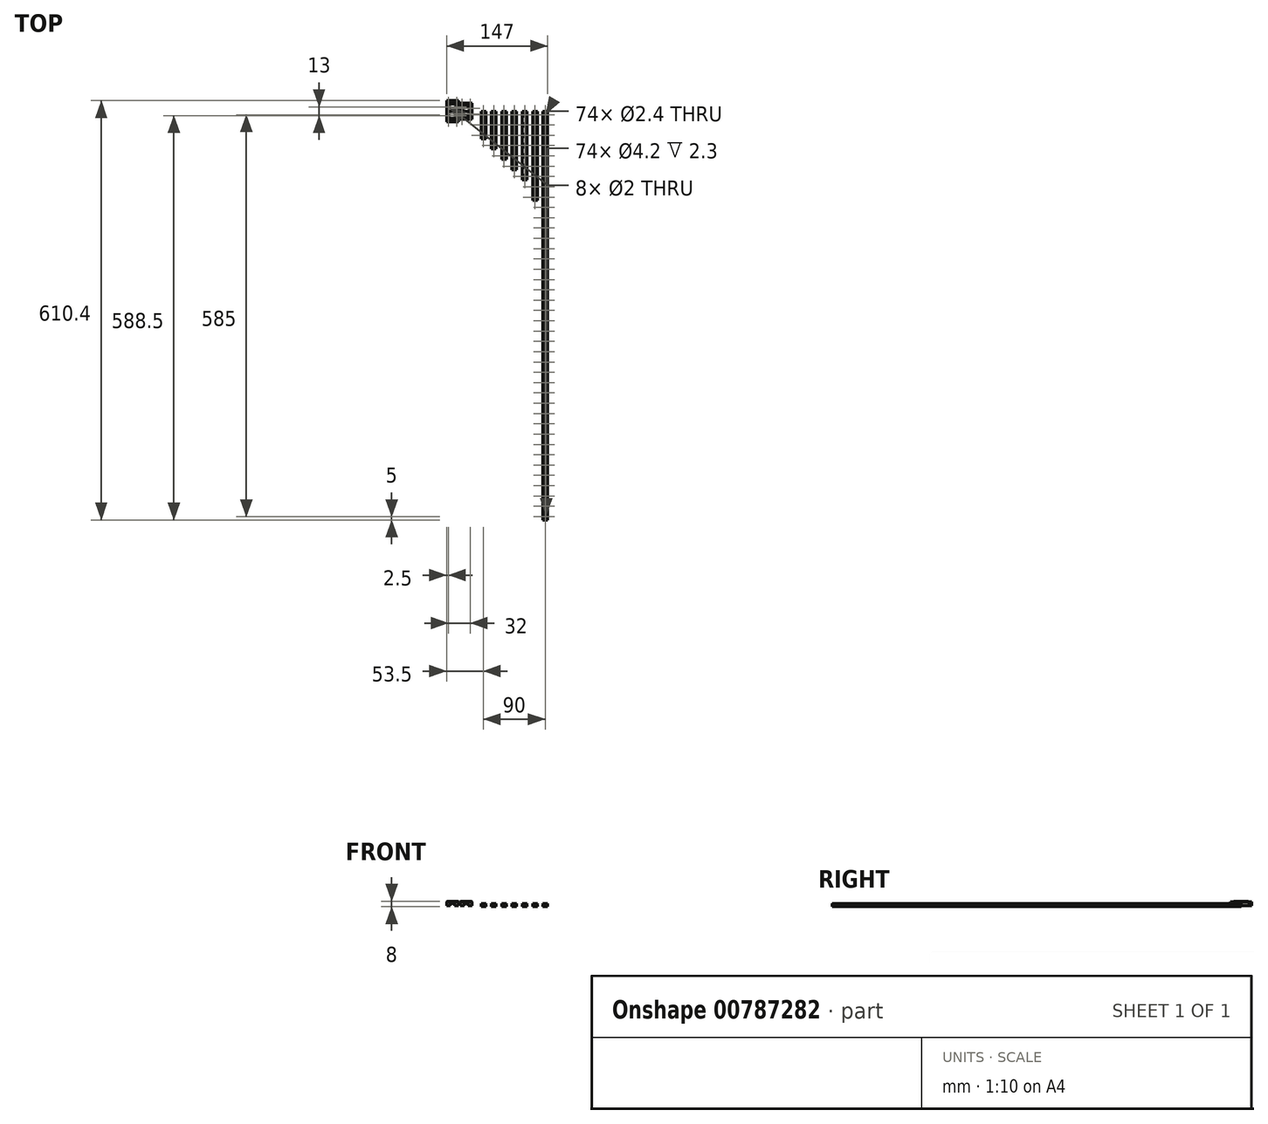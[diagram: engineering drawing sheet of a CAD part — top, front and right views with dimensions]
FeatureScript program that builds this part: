
annotation { "Feature Type Name" : "Feature", "Feature Type Description" : "" }
export const myFeature = defineFeature(function(context is Context, id is Id, definition is map)
    precondition{}
    {
        {
            var Q0;
            Q0=qCreatedBy(makeId("Front.planeOp"),FACE);
            var sketch = newSketch(context, id + "F0", { "sketchPlane" : qUnion([Q0])});
            skPoint(sketch, "E0.middle", {"position": v(0, 0) * mm});
            skLineSegment(sketch, "E1.bottom", {"start": v(3.22, -2.4) * mm, "end": v(-3.22, -2.4) * mm});
            skLineSegment(sketch, "E1.top", {"start": v(3.22, 2.4) * mm, "end": v(-3.22, 2.4) * mm});
            skLineSegment(sketch, "E1.left", {"start": v(3.5, -2.12) * mm, "end": v(3.5, 0.1) * mm});
            skLineSegment(sketch, "E1.right", {"start": v(-3.5, -2.12) * mm, "end": v(-3.5, 0.1) * mm});
            skArc(sketch, "E2", {"start": v(-3.5, 0.1) * mm, "mid": v(-3.23, 0.26) * mm, "end": v(-3.04, 0.51) * mm});
            skArc(sketch, "E3", {"start": v(3.5, 1.58) * mm, "mid": v(3.23, 1.42) * mm, "end": v(3.04, 1.17) * mm});
            skLineSegment(sketch, "E4", {"start": v(2.6, 1.16) * mm, "end": v(3.04, 1.16) * mm});
            skLineSegment(sketch, "E5", {"start": v(2.6, 0.51) * mm, "end": v(3.04, 0.51) * mm});
            skLineSegment(sketch, "E6", {"start": v(-2.6, 0.51) * mm, "end": v(-3.04, 0.51) * mm});
            skLineSegment(sketch, "E7", {"start": v(-2.6, 1.16) * mm, "end": v(-3.04, 1.16) * mm});
            skLineSegment(sketch, "E8", {"start": v(-3.5, 2.12) * mm, "end": v(-3.22, 2.4) * mm});
            skLineSegment(sketch, "E9.MirrorCS", {"start": v(3.5, 2.12) * mm, "end": v(3.22, 2.4) * mm});
            skLineSegment(sketch, "E10.MirrorCS", {"start": v(3.5, -2.12) * mm, "end": v(3.22, -2.4) * mm});
            skLineSegment(sketch, "E11.MirrorCS", {"start": v(-3.5, -2.12) * mm, "end": v(-3.22, -2.4) * mm});
            skPoint(sketch, "E12.orphan", {"position": v(-3.5, 2.4) * mm});
            skLineSegment(sketch, "E13.trimOffspring", {"start": v(-3.5, 1.58) * mm, "end": v(-3.5, 2.12) * mm});
            skArc(sketch, "E14.trimOffspring", {"start": v(-3.04, 1.17) * mm, "mid": v(-3.23, 1.42) * mm, "end": v(-3.5, 1.58) * mm});
            skPoint(sketch, "E15.orphan", {"position": v(3.5, 2.4) * mm});
            skLineSegment(sketch, "E16.trimOffspring", {"start": v(3.5, 1.58) * mm, "end": v(3.5, 2.12) * mm});
            skArc(sketch, "E17.trimOffspring", {"start": v(3.04, 0.51) * mm, "mid": v(3.23, 0.26) * mm, "end": v(3.5, 0.1) * mm});
            skPoint(sketch, "E18.orphan", {"position": v(3.5, -2.4) * mm});
            skPoint(sketch, "E19.orphan", {"position": v(-3.5, -2.4) * mm});
            skLineSegment(sketch, "E20", {"start": v(-2.6, 1.16) * mm, "end": v(-2.6, 0.51) * mm});
            skLineSegment(sketch, "E21", {"start": v(2.6, 1.16) * mm, "end": v(2.6, 0.51) * mm});
            skLineSegment(sketch, "E22", {"start": v(-3.74, 0.84) * mm, "end": v(3.74, 0.84) * mm, "construction": true});
            skLineSegment(sketch, "E23.1.0.0", {"start": v(11.26, 0.84) * mm, "end": v(18.74, 0.84) * mm, "construction": true});
            skLineSegment(sketch, "E23.1.0.1", {"start": v(11.5, -2.12) * mm, "end": v(11.5, 0.1) * mm});
            skLineSegment(sketch, "E23.1.0.2", {"start": v(18.5, -2.12) * mm, "end": v(18.5, 0.1) * mm});
            skLineSegment(sketch, "E23.1.0.3", {"start": v(18.22, -2.4) * mm, "end": v(11.78, -2.4) * mm});
            skLineSegment(sketch, "E23.1.0.4", {"start": v(18.22, 2.4) * mm, "end": v(11.78, 2.4) * mm});
            skPoint(sketch, "E23.1.0.5", {"position": v(15, 0) * mm});
            skPoint(sketch, "E23.1.0.6", {"position": v(11.5, -2.4) * mm});
            skPoint(sketch, "E23.1.0.7", {"position": v(11.5, 2.4) * mm});
            skPoint(sketch, "E23.1.0.8", {"position": v(18.5, 2.4) * mm});
            skPoint(sketch, "E23.1.0.9", {"position": v(18.5, -2.4) * mm});
            skPoint(sketch, "E23.1.0.10", {"position": v(15, 0) * mm});
            skLineSegment(sketch, "E23.1.0.11", {"start": v(18.5, -2.12) * mm, "end": v(18.22, -2.4) * mm});
            skLineSegment(sketch, "E23.1.0.12", {"start": v(18.5, 2.12) * mm, "end": v(18.22, 2.4) * mm});
            skLineSegment(sketch, "E23.1.0.13", {"start": v(11.5, -2.12) * mm, "end": v(11.78, -2.4) * mm});
            skLineSegment(sketch, "E23.1.0.14", {"start": v(12.4, 1.16) * mm, "end": v(11.96, 1.16) * mm});
            skLineSegment(sketch, "E23.1.0.15", {"start": v(11.5, 1.58) * mm, "end": v(11.5, 2.12) * mm});
            skLineSegment(sketch, "E23.1.0.16", {"start": v(18.5, 1.58) * mm, "end": v(18.5, 2.12) * mm});
            skArc(sketch, "E23.1.0.17", {"start": v(18.04, 0.51) * mm, "mid": v(18.23, 0.26) * mm, "end": v(18.5, 0.1) * mm});
            skLineSegment(sketch, "E23.1.0.18", {"start": v(12.4, 1.16) * mm, "end": v(12.4, 0.51) * mm});
            skLineSegment(sketch, "E23.1.0.19", {"start": v(17.6, 0.51) * mm, "end": v(18.04, 0.51) * mm});
            skLineSegment(sketch, "E23.1.0.20", {"start": v(12.4, 0.51) * mm, "end": v(11.96, 0.51) * mm});
            skArc(sketch, "E23.1.0.21", {"start": v(11.5, 0.1) * mm, "mid": v(11.77, 0.26) * mm, "end": v(11.96, 0.51) * mm});
            skLineSegment(sketch, "E23.1.0.22", {"start": v(11.5, 2.12) * mm, "end": v(11.78, 2.4) * mm});
            skArc(sketch, "E23.1.0.23", {"start": v(11.96, 1.17) * mm, "mid": v(11.77, 1.42) * mm, "end": v(11.5, 1.58) * mm});
            skLineSegment(sketch, "E23.1.0.24", {"start": v(17.6, 1.16) * mm, "end": v(18.04, 1.16) * mm});
            skArc(sketch, "E23.1.0.25", {"start": v(18.5, 1.58) * mm, "mid": v(18.23, 1.42) * mm, "end": v(18.04, 1.17) * mm});
            skArc(sketch, "E23.1.0.26", {"start": v(18.04, 0.51) * mm, "mid": v(18.23, 0.26) * mm, "end": v(18.5, 0.1) * mm});
            skLineSegment(sketch, "E23.1.0.27", {"start": v(17.6, 1.16) * mm, "end": v(17.6, 0.51) * mm});
            skLineSegment(sketch, "E23.2.0.0", {"start": v(26.26, 0.84) * mm, "end": v(33.74, 0.84) * mm, "construction": true});
            skLineSegment(sketch, "E23.2.0.1", {"start": v(26.5, -2.12) * mm, "end": v(26.5, 0.1) * mm});
            skLineSegment(sketch, "E23.2.0.2", {"start": v(33.5, -2.12) * mm, "end": v(33.5, 0.1) * mm});
            skLineSegment(sketch, "E23.2.0.3", {"start": v(33.22, -2.4) * mm, "end": v(26.78, -2.4) * mm});
            skLineSegment(sketch, "E23.2.0.4", {"start": v(33.22, 2.4) * mm, "end": v(26.78, 2.4) * mm});
            skPoint(sketch, "E23.2.0.5", {"position": v(30, 0) * mm});
            skPoint(sketch, "E23.2.0.6", {"position": v(26.5, -2.4) * mm});
            skPoint(sketch, "E23.2.0.7", {"position": v(26.5, 2.4) * mm});
            skPoint(sketch, "E23.2.0.8", {"position": v(33.5, 2.4) * mm});
            skPoint(sketch, "E23.2.0.9", {"position": v(33.5, -2.4) * mm});
            skPoint(sketch, "E23.2.0.10", {"position": v(30, 0) * mm});
            skLineSegment(sketch, "E23.2.0.11", {"start": v(33.5, -2.12) * mm, "end": v(33.22, -2.4) * mm});
            skLineSegment(sketch, "E23.2.0.12", {"start": v(33.5, 2.12) * mm, "end": v(33.22, 2.4) * mm});
            skLineSegment(sketch, "E23.2.0.13", {"start": v(26.5, -2.12) * mm, "end": v(26.78, -2.4) * mm});
            skLineSegment(sketch, "E23.2.0.14", {"start": v(27.4, 1.16) * mm, "end": v(26.96, 1.16) * mm});
            skLineSegment(sketch, "E23.2.0.15", {"start": v(26.5, 1.58) * mm, "end": v(26.5, 2.12) * mm});
            skLineSegment(sketch, "E23.2.0.16", {"start": v(33.5, 1.58) * mm, "end": v(33.5, 2.12) * mm});
            skArc(sketch, "E23.2.0.17", {"start": v(33.04, 0.51) * mm, "mid": v(33.23, 0.26) * mm, "end": v(33.5, 0.1) * mm});
            skLineSegment(sketch, "E23.2.0.18", {"start": v(27.4, 1.16) * mm, "end": v(27.4, 0.51) * mm});
            skLineSegment(sketch, "E23.2.0.19", {"start": v(32.6, 0.51) * mm, "end": v(33.04, 0.51) * mm});
            skLineSegment(sketch, "E23.2.0.20", {"start": v(27.4, 0.51) * mm, "end": v(26.96, 0.51) * mm});
            skArc(sketch, "E23.2.0.21", {"start": v(26.5, 0.1) * mm, "mid": v(26.77, 0.26) * mm, "end": v(26.96, 0.51) * mm});
            skLineSegment(sketch, "E23.2.0.22", {"start": v(26.5, 2.12) * mm, "end": v(26.78, 2.4) * mm});
            skArc(sketch, "E23.2.0.23", {"start": v(26.96, 1.17) * mm, "mid": v(26.77, 1.42) * mm, "end": v(26.5, 1.58) * mm});
            skLineSegment(sketch, "E23.2.0.24", {"start": v(32.6, 1.16) * mm, "end": v(33.04, 1.16) * mm});
            skArc(sketch, "E23.2.0.25", {"start": v(33.5, 1.58) * mm, "mid": v(33.23, 1.42) * mm, "end": v(33.04, 1.17) * mm});
            skArc(sketch, "E23.2.0.26", {"start": v(33.04, 0.51) * mm, "mid": v(33.23, 0.26) * mm, "end": v(33.5, 0.1) * mm});
            skLineSegment(sketch, "E23.2.0.27", {"start": v(32.6, 1.16) * mm, "end": v(32.6, 0.51) * mm});
            skLineSegment(sketch, "E23.3.0.0", {"start": v(41.26, 0.84) * mm, "end": v(48.74, 0.84) * mm, "construction": true});
            skLineSegment(sketch, "E23.3.0.1", {"start": v(41.5, -2.12) * mm, "end": v(41.5, 0.1) * mm});
            skLineSegment(sketch, "E23.3.0.2", {"start": v(48.5, -2.12) * mm, "end": v(48.5, 0.1) * mm});
            skLineSegment(sketch, "E23.3.0.3", {"start": v(48.22, -2.4) * mm, "end": v(41.78, -2.4) * mm});
            skLineSegment(sketch, "E23.3.0.4", {"start": v(48.22, 2.4) * mm, "end": v(41.78, 2.4) * mm});
            skPoint(sketch, "E23.3.0.5", {"position": v(45, 0) * mm});
            skPoint(sketch, "E23.3.0.6", {"position": v(41.5, -2.4) * mm});
            skPoint(sketch, "E23.3.0.7", {"position": v(41.5, 2.4) * mm});
            skPoint(sketch, "E23.3.0.8", {"position": v(48.5, 2.4) * mm});
            skPoint(sketch, "E23.3.0.9", {"position": v(48.5, -2.4) * mm});
            skPoint(sketch, "E23.3.0.10", {"position": v(45, 0) * mm});
            skLineSegment(sketch, "E23.3.0.11", {"start": v(48.5, -2.12) * mm, "end": v(48.22, -2.4) * mm});
            skLineSegment(sketch, "E23.3.0.12", {"start": v(48.5, 2.12) * mm, "end": v(48.22, 2.4) * mm});
            skLineSegment(sketch, "E23.3.0.13", {"start": v(41.5, -2.12) * mm, "end": v(41.78, -2.4) * mm});
            skLineSegment(sketch, "E23.3.0.14", {"start": v(42.4, 1.16) * mm, "end": v(41.96, 1.16) * mm});
            skLineSegment(sketch, "E23.3.0.15", {"start": v(41.5, 1.58) * mm, "end": v(41.5, 2.12) * mm});
            skLineSegment(sketch, "E23.3.0.16", {"start": v(48.5, 1.58) * mm, "end": v(48.5, 2.12) * mm});
            skArc(sketch, "E23.3.0.17", {"start": v(48.04, 0.51) * mm, "mid": v(48.23, 0.26) * mm, "end": v(48.5, 0.1) * mm});
            skLineSegment(sketch, "E23.3.0.18", {"start": v(42.4, 1.16) * mm, "end": v(42.4, 0.51) * mm});
            skLineSegment(sketch, "E23.3.0.19", {"start": v(47.6, 0.51) * mm, "end": v(48.04, 0.51) * mm});
            skLineSegment(sketch, "E23.3.0.20", {"start": v(42.4, 0.51) * mm, "end": v(41.96, 0.51) * mm});
            skArc(sketch, "E23.3.0.21", {"start": v(41.5, 0.1) * mm, "mid": v(41.77, 0.26) * mm, "end": v(41.96, 0.51) * mm});
            skLineSegment(sketch, "E23.3.0.22", {"start": v(41.5, 2.12) * mm, "end": v(41.78, 2.4) * mm});
            skArc(sketch, "E23.3.0.23", {"start": v(41.96, 1.17) * mm, "mid": v(41.77, 1.42) * mm, "end": v(41.5, 1.58) * mm});
            skLineSegment(sketch, "E23.3.0.24", {"start": v(47.6, 1.16) * mm, "end": v(48.04, 1.16) * mm});
            skArc(sketch, "E23.3.0.25", {"start": v(48.5, 1.58) * mm, "mid": v(48.23, 1.42) * mm, "end": v(48.04, 1.17) * mm});
            skArc(sketch, "E23.3.0.26", {"start": v(48.04, 0.51) * mm, "mid": v(48.23, 0.26) * mm, "end": v(48.5, 0.1) * mm});
            skLineSegment(sketch, "E23.3.0.27", {"start": v(47.6, 1.16) * mm, "end": v(47.6, 0.51) * mm});
            skLineSegment(sketch, "E23.4.0.0", {"start": v(56.26, 0.84) * mm, "end": v(63.74, 0.84) * mm, "construction": true});
            skLineSegment(sketch, "E23.4.0.1", {"start": v(56.5, -2.12) * mm, "end": v(56.5, 0.1) * mm});
            skLineSegment(sketch, "E23.4.0.2", {"start": v(63.5, -2.12) * mm, "end": v(63.5, 0.1) * mm});
            skLineSegment(sketch, "E23.4.0.3", {"start": v(63.22, -2.4) * mm, "end": v(56.78, -2.4) * mm});
            skLineSegment(sketch, "E23.4.0.4", {"start": v(63.22, 2.4) * mm, "end": v(56.78, 2.4) * mm});
            skPoint(sketch, "E23.4.0.5", {"position": v(60, 0) * mm});
            skPoint(sketch, "E23.4.0.6", {"position": v(56.5, -2.4) * mm});
            skPoint(sketch, "E23.4.0.7", {"position": v(56.5, 2.4) * mm});
            skPoint(sketch, "E23.4.0.8", {"position": v(63.5, 2.4) * mm});
            skPoint(sketch, "E23.4.0.9", {"position": v(63.5, -2.4) * mm});
            skPoint(sketch, "E23.4.0.10", {"position": v(60, 0) * mm});
            skLineSegment(sketch, "E23.4.0.11", {"start": v(63.5, -2.12) * mm, "end": v(63.22, -2.4) * mm});
            skLineSegment(sketch, "E23.4.0.12", {"start": v(63.5, 2.12) * mm, "end": v(63.22, 2.4) * mm});
            skLineSegment(sketch, "E23.4.0.13", {"start": v(56.5, -2.12) * mm, "end": v(56.78, -2.4) * mm});
            skLineSegment(sketch, "E23.4.0.14", {"start": v(57.4, 1.16) * mm, "end": v(56.96, 1.16) * mm});
            skLineSegment(sketch, "E23.4.0.15", {"start": v(56.5, 1.58) * mm, "end": v(56.5, 2.12) * mm});
            skLineSegment(sketch, "E23.4.0.16", {"start": v(63.5, 1.58) * mm, "end": v(63.5, 2.12) * mm});
            skArc(sketch, "E23.4.0.17", {"start": v(63.04, 0.51) * mm, "mid": v(63.23, 0.26) * mm, "end": v(63.5, 0.1) * mm});
            skLineSegment(sketch, "E23.4.0.18", {"start": v(57.4, 1.16) * mm, "end": v(57.4, 0.51) * mm});
            skLineSegment(sketch, "E23.4.0.19", {"start": v(62.6, 0.51) * mm, "end": v(63.04, 0.51) * mm});
            skLineSegment(sketch, "E23.4.0.20", {"start": v(57.4, 0.51) * mm, "end": v(56.96, 0.51) * mm});
            skArc(sketch, "E23.4.0.21", {"start": v(56.5, 0.1) * mm, "mid": v(56.77, 0.26) * mm, "end": v(56.96, 0.51) * mm});
            skLineSegment(sketch, "E23.4.0.22", {"start": v(56.5, 2.12) * mm, "end": v(56.78, 2.4) * mm});
            skArc(sketch, "E23.4.0.23", {"start": v(56.96, 1.17) * mm, "mid": v(56.77, 1.42) * mm, "end": v(56.5, 1.58) * mm});
            skLineSegment(sketch, "E23.4.0.24", {"start": v(62.6, 1.16) * mm, "end": v(63.04, 1.16) * mm});
            skArc(sketch, "E23.4.0.25", {"start": v(63.5, 1.58) * mm, "mid": v(63.23, 1.42) * mm, "end": v(63.04, 1.17) * mm});
            skArc(sketch, "E23.4.0.26", {"start": v(63.04, 0.51) * mm, "mid": v(63.23, 0.26) * mm, "end": v(63.5, 0.1) * mm});
            skLineSegment(sketch, "E23.4.0.27", {"start": v(62.6, 1.16) * mm, "end": v(62.6, 0.51) * mm});
            skLineSegment(sketch, "E23.5.0.0", {"start": v(71.26, 0.84) * mm, "end": v(78.74, 0.84) * mm, "construction": true});
            skLineSegment(sketch, "E23.5.0.1", {"start": v(71.5, -2.12) * mm, "end": v(71.5, 0.1) * mm});
            skLineSegment(sketch, "E23.5.0.2", {"start": v(78.5, -2.12) * mm, "end": v(78.5, 0.1) * mm});
            skLineSegment(sketch, "E23.5.0.3", {"start": v(78.22, -2.4) * mm, "end": v(71.78, -2.4) * mm});
            skLineSegment(sketch, "E23.5.0.4", {"start": v(78.22, 2.4) * mm, "end": v(71.78, 2.4) * mm});
            skPoint(sketch, "E23.5.0.5", {"position": v(75, 0) * mm});
            skPoint(sketch, "E23.5.0.6", {"position": v(71.5, -2.4) * mm});
            skPoint(sketch, "E23.5.0.7", {"position": v(71.5, 2.4) * mm});
            skPoint(sketch, "E23.5.0.8", {"position": v(78.5, 2.4) * mm});
            skPoint(sketch, "E23.5.0.9", {"position": v(78.5, -2.4) * mm});
            skPoint(sketch, "E23.5.0.10", {"position": v(75, 0) * mm});
            skLineSegment(sketch, "E23.5.0.11", {"start": v(78.5, -2.12) * mm, "end": v(78.22, -2.4) * mm});
            skLineSegment(sketch, "E23.5.0.12", {"start": v(78.5, 2.12) * mm, "end": v(78.22, 2.4) * mm});
            skLineSegment(sketch, "E23.5.0.13", {"start": v(71.5, -2.12) * mm, "end": v(71.78, -2.4) * mm});
            skLineSegment(sketch, "E23.5.0.14", {"start": v(72.4, 1.16) * mm, "end": v(71.96, 1.16) * mm});
            skLineSegment(sketch, "E23.5.0.15", {"start": v(71.5, 1.58) * mm, "end": v(71.5, 2.12) * mm});
            skLineSegment(sketch, "E23.5.0.16", {"start": v(78.5, 1.58) * mm, "end": v(78.5, 2.12) * mm});
            skArc(sketch, "E23.5.0.17", {"start": v(78.04, 0.51) * mm, "mid": v(78.23, 0.26) * mm, "end": v(78.5, 0.1) * mm});
            skLineSegment(sketch, "E23.5.0.18", {"start": v(72.4, 1.16) * mm, "end": v(72.4, 0.51) * mm});
            skLineSegment(sketch, "E23.5.0.19", {"start": v(77.6, 0.51) * mm, "end": v(78.04, 0.51) * mm});
            skLineSegment(sketch, "E23.5.0.20", {"start": v(72.4, 0.51) * mm, "end": v(71.96, 0.51) * mm});
            skArc(sketch, "E23.5.0.21", {"start": v(71.5, 0.1) * mm, "mid": v(71.77, 0.26) * mm, "end": v(71.96, 0.51) * mm});
            skLineSegment(sketch, "E23.5.0.22", {"start": v(71.5, 2.12) * mm, "end": v(71.78, 2.4) * mm});
            skArc(sketch, "E23.5.0.23", {"start": v(71.96, 1.17) * mm, "mid": v(71.77, 1.42) * mm, "end": v(71.5, 1.58) * mm});
            skLineSegment(sketch, "E23.5.0.24", {"start": v(77.6, 1.16) * mm, "end": v(78.04, 1.16) * mm});
            skArc(sketch, "E23.5.0.25", {"start": v(78.5, 1.58) * mm, "mid": v(78.23, 1.42) * mm, "end": v(78.04, 1.17) * mm});
            skArc(sketch, "E23.5.0.26", {"start": v(78.04, 0.51) * mm, "mid": v(78.23, 0.26) * mm, "end": v(78.5, 0.1) * mm});
            skLineSegment(sketch, "E23.5.0.27", {"start": v(77.6, 1.16) * mm, "end": v(77.6, 0.51) * mm});
            skLineSegment(sketch, "E23.6.0.0", {"start": v(86.26, 0.84) * mm, "end": v(93.74, 0.84) * mm, "construction": true});
            skLineSegment(sketch, "E23.6.0.1", {"start": v(86.5, -2.12) * mm, "end": v(86.5, 0.1) * mm});
            skLineSegment(sketch, "E23.6.0.2", {"start": v(93.5, -2.12) * mm, "end": v(93.5, 0.1) * mm});
            skLineSegment(sketch, "E23.6.0.3", {"start": v(93.22, -2.4) * mm, "end": v(86.78, -2.4) * mm});
            skLineSegment(sketch, "E23.6.0.4", {"start": v(93.22, 2.4) * mm, "end": v(86.78, 2.4) * mm});
            skPoint(sketch, "E23.6.0.5", {"position": v(90, 0) * mm});
            skPoint(sketch, "E23.6.0.6", {"position": v(86.5, -2.4) * mm});
            skPoint(sketch, "E23.6.0.7", {"position": v(86.5, 2.4) * mm});
            skPoint(sketch, "E23.6.0.8", {"position": v(93.5, 2.4) * mm});
            skPoint(sketch, "E23.6.0.9", {"position": v(93.5, -2.4) * mm});
            skPoint(sketch, "E23.6.0.10", {"position": v(90, 0) * mm});
            skLineSegment(sketch, "E23.6.0.11", {"start": v(93.5, -2.12) * mm, "end": v(93.22, -2.4) * mm});
            skLineSegment(sketch, "E23.6.0.12", {"start": v(93.5, 2.12) * mm, "end": v(93.22, 2.4) * mm});
            skLineSegment(sketch, "E23.6.0.13", {"start": v(86.5, -2.12) * mm, "end": v(86.78, -2.4) * mm});
            skLineSegment(sketch, "E23.6.0.14", {"start": v(87.4, 1.16) * mm, "end": v(86.96, 1.16) * mm});
            skLineSegment(sketch, "E23.6.0.15", {"start": v(86.5, 1.58) * mm, "end": v(86.5, 2.12) * mm});
            skLineSegment(sketch, "E23.6.0.16", {"start": v(93.5, 1.58) * mm, "end": v(93.5, 2.12) * mm});
            skArc(sketch, "E23.6.0.17", {"start": v(93.04, 0.51) * mm, "mid": v(93.23, 0.26) * mm, "end": v(93.5, 0.1) * mm});
            skLineSegment(sketch, "E23.6.0.18", {"start": v(87.4, 1.16) * mm, "end": v(87.4, 0.51) * mm});
            skLineSegment(sketch, "E23.6.0.19", {"start": v(92.6, 0.51) * mm, "end": v(93.04, 0.51) * mm});
            skLineSegment(sketch, "E23.6.0.20", {"start": v(87.4, 0.51) * mm, "end": v(86.96, 0.51) * mm});
            skArc(sketch, "E23.6.0.21", {"start": v(86.5, 0.1) * mm, "mid": v(86.77, 0.26) * mm, "end": v(86.96, 0.51) * mm});
            skLineSegment(sketch, "E23.6.0.22", {"start": v(86.5, 2.12) * mm, "end": v(86.78, 2.4) * mm});
            skArc(sketch, "E23.6.0.23", {"start": v(86.96, 1.17) * mm, "mid": v(86.77, 1.42) * mm, "end": v(86.5, 1.58) * mm});
            skLineSegment(sketch, "E23.6.0.24", {"start": v(92.6, 1.16) * mm, "end": v(93.04, 1.16) * mm});
            skArc(sketch, "E23.6.0.25", {"start": v(93.5, 1.58) * mm, "mid": v(93.23, 1.42) * mm, "end": v(93.04, 1.17) * mm});
            skArc(sketch, "E23.6.0.26", {"start": v(93.04, 0.51) * mm, "mid": v(93.23, 0.26) * mm, "end": v(93.5, 0.1) * mm});
            skLineSegment(sketch, "E23.6.0.27", {"start": v(92.6, 1.16) * mm, "end": v(92.6, 0.51) * mm});
            skLineSegment(sketch, "E23.direction1", {"start": v(-3.5, -2.4) * mm, "end": v(11.5, -2.4) * mm, "construction": true});
            skSolve(sketch);
        }
        {
            var Q0;
            Q0=makeQuery(id+"F0.imprint","IMPRINT",FACE,{"disambiguationData":[TD([[makeQuery(id+"F0.imprint","IMPRINT",EDGE,{"derivedFrom":sQuery(id+"F0.wireOp",EDGE,"E1.bottom")}),-1.0]])]});
            extrude(context, id + "F1", {"entities" : qUnion([Q0]), "depth" : 40 * mm, "offsetDistance" : 25 * mm});
        }
        {
            var Q0;
            Q0=makeQuery(id+"F0.imprint","IMPRINT",FACE,{"disambiguationData":[TD([[makeQuery(id+"F0.imprint","IMPRINT",EDGE,{"derivedFrom":sQuery(id+"F0.wireOp",EDGE,"E23.1.0.1")}),-1.0]])]});
            extrude(context, id + "F2", {"entities" : qUnion([Q0]), "depth" : 55 * mm, "offsetDistance" : 25 * mm});
        }
        {
            var Q0;
            Q0=makeQuery(id+"F0.imprint","IMPRINT",FACE,{"disambiguationData":[TD([[makeQuery(id+"F0.imprint","IMPRINT",EDGE,{"derivedFrom":sQuery(id+"F0.wireOp",EDGE,"E23.2.0.1")}),-1.0]])]});
            extrude(context, id + "F3", {"entities" : qUnion([Q0]), "depth" : 70 * mm, "offsetDistance" : 25 * mm});
        }
        {
            var Q0;
            Q0=makeQuery(id+"F0.imprint","IMPRINT",FACE,{"disambiguationData":[TD([[makeQuery(id+"F0.imprint","IMPRINT",EDGE,{"derivedFrom":sQuery(id+"F0.wireOp",EDGE,"E23.3.0.1")}),-1.0]])]});
            extrude(context, id + "F4", {"entities" : qUnion([Q0]), "depth" : 85 * mm, "offsetDistance" : 25 * mm});
        }
        {
            var Q0;
            Q0=makeQuery(id+"F0.imprint","IMPRINT",FACE,{"disambiguationData":[TD([[makeQuery(id+"F0.imprint","IMPRINT",EDGE,{"derivedFrom":sQuery(id+"F0.wireOp",EDGE,"E23.4.0.1")}),-1.0]])]});
            extrude(context, id + "F5", {"entities" : qUnion([Q0]), "depth" : 100 * mm, "offsetDistance" : 25 * mm});
        }
        {
            var Q0;
            Q0=makeQuery(id+"F0.imprint","IMPRINT",FACE,{"disambiguationData":[TD([[makeQuery(id+"F0.imprint","IMPRINT",EDGE,{"derivedFrom":sQuery(id+"F0.wireOp",EDGE,"E23.5.0.1")}),-1.0]])]});
            extrude(context, id + "F6", {"entities" : qUnion([Q0]), "depth" : 130 * mm, "offsetDistance" : 25 * mm});
        }
        {
            var Q0;
            Q0=makeQuery(id+"F0.imprint","IMPRINT",FACE,{"disambiguationData":[TD([[makeQuery(id+"F0.imprint","IMPRINT",EDGE,{"derivedFrom":sQuery(id+"F0.wireOp",EDGE,"E23.6.0.1")}),-1.0]])]});
            extrude(context, id + "F7", {"entities" : qUnion([Q0]), "depth" : 595 * mm, "offsetDistance" : 25 * mm});
        }
        {
            var Q0;
            Q0=makeQuery(id+"F1.opExtrude","SWEPT_FACE",FACE,{"disambiguationData":[OSD([sQuery(id+"F0.wireOp",EDGE,"E1.top")])]});
            var sketch = newSketch(context, id + "F8", { "sketchPlane" : qUnion([Q0])});
            skPoint(sketch, "E24", {"position": v(0, -5) * mm});
            skPoint(sketch, "E25.1.0.0", {"position": v(15, -5) * mm});
            skPoint(sketch, "E25.2.0.0", {"position": v(30, -5) * mm});
            skPoint(sketch, "E25.3.0.0", {"position": v(45, -5) * mm});
            skPoint(sketch, "E25.4.0.0", {"position": v(60, -5) * mm});
            skPoint(sketch, "E25.5.0.0", {"position": v(75, -5) * mm});
            skPoint(sketch, "E25.6.0.0", {"position": v(90, -5) * mm});
            skLineSegment(sketch, "E25.direction1", {"start": v(0, -5) * mm, "end": v(15, -5) * mm, "construction": true});
            skPoint(sketch, "E26.1.0.0", {"position": v(0, -20) * mm});
            skPoint(sketch, "E26.1.0.1", {"position": v(15, -20) * mm});
            skPoint(sketch, "E26.1.0.2", {"position": v(30, -20) * mm});
            skPoint(sketch, "E26.1.0.3", {"position": v(45, -20) * mm});
            skPoint(sketch, "E26.1.0.4", {"position": v(60, -20) * mm});
            skPoint(sketch, "E26.1.0.5", {"position": v(75, -20) * mm});
            skPoint(sketch, "E26.1.0.6", {"position": v(90, -20) * mm});
            skPoint(sketch, "E26.2.0.0", {"position": v(0, -35) * mm});
            skPoint(sketch, "E26.2.0.1", {"position": v(15, -35) * mm});
            skPoint(sketch, "E26.2.0.2", {"position": v(30, -35) * mm});
            skPoint(sketch, "E26.2.0.3", {"position": v(45, -35) * mm});
            skPoint(sketch, "E26.2.0.4", {"position": v(60, -35) * mm});
            skPoint(sketch, "E26.2.0.5", {"position": v(75, -35) * mm});
            skPoint(sketch, "E26.2.0.6", {"position": v(90, -35) * mm});
            skPoint(sketch, "E26.3.0.0", {"position": v(0, -50) * mm});
            skPoint(sketch, "E26.3.0.1", {"position": v(15, -50) * mm});
            skPoint(sketch, "E26.3.0.2", {"position": v(30, -50) * mm});
            skPoint(sketch, "E26.3.0.3", {"position": v(45, -50) * mm});
            skPoint(sketch, "E26.3.0.4", {"position": v(60, -50) * mm});
            skPoint(sketch, "E26.3.0.5", {"position": v(75, -50) * mm});
            skPoint(sketch, "E26.3.0.6", {"position": v(90, -50) * mm});
            skPoint(sketch, "E26.4.0.0", {"position": v(0, -65) * mm});
            skPoint(sketch, "E26.4.0.1", {"position": v(15, -65) * mm});
            skPoint(sketch, "E26.4.0.2", {"position": v(30, -65) * mm});
            skPoint(sketch, "E26.4.0.3", {"position": v(45, -65) * mm});
            skPoint(sketch, "E26.4.0.4", {"position": v(60, -65) * mm});
            skPoint(sketch, "E26.4.0.5", {"position": v(75, -65) * mm});
            skPoint(sketch, "E26.4.0.6", {"position": v(90, -65) * mm});
            skPoint(sketch, "E26.5.0.0", {"position": v(0, -80) * mm});
            skPoint(sketch, "E26.5.0.1", {"position": v(15, -80) * mm});
            skPoint(sketch, "E26.5.0.2", {"position": v(30, -80) * mm});
            skPoint(sketch, "E26.5.0.3", {"position": v(45, -80) * mm});
            skPoint(sketch, "E26.5.0.4", {"position": v(60, -80) * mm});
            skPoint(sketch, "E26.5.0.5", {"position": v(75, -80) * mm});
            skPoint(sketch, "E26.5.0.6", {"position": v(90, -80) * mm});
            skPoint(sketch, "E26.6.0.0", {"position": v(0, -95) * mm});
            skPoint(sketch, "E26.6.0.1", {"position": v(15, -95) * mm});
            skPoint(sketch, "E26.6.0.2", {"position": v(30, -95) * mm});
            skPoint(sketch, "E26.6.0.3", {"position": v(45, -95) * mm});
            skPoint(sketch, "E26.6.0.4", {"position": v(60, -95) * mm});
            skPoint(sketch, "E26.6.0.5", {"position": v(75, -95) * mm});
            skPoint(sketch, "E26.6.0.6", {"position": v(90, -95) * mm});
            skPoint(sketch, "E26.7.0.0", {"position": v(0, -110) * mm});
            skPoint(sketch, "E26.7.0.1", {"position": v(15, -110) * mm});
            skPoint(sketch, "E26.7.0.2", {"position": v(30, -110) * mm});
            skPoint(sketch, "E26.7.0.3", {"position": v(45, -110) * mm});
            skPoint(sketch, "E26.7.0.4", {"position": v(60, -110) * mm});
            skPoint(sketch, "E26.7.0.5", {"position": v(75, -110) * mm});
            skPoint(sketch, "E26.7.0.6", {"position": v(90, -110) * mm});
            skPoint(sketch, "E26.8.0.0", {"position": v(0, -125) * mm});
            skPoint(sketch, "E26.8.0.1", {"position": v(15, -125) * mm});
            skPoint(sketch, "E26.8.0.2", {"position": v(30, -125) * mm});
            skPoint(sketch, "E26.8.0.3", {"position": v(45, -125) * mm});
            skPoint(sketch, "E26.8.0.4", {"position": v(60, -125) * mm});
            skPoint(sketch, "E26.8.0.5", {"position": v(75, -125) * mm});
            skPoint(sketch, "E26.8.0.6", {"position": v(90, -125) * mm});
            skPoint(sketch, "E26.9.0.0", {"position": v(0, -140) * mm});
            skPoint(sketch, "E26.9.0.1", {"position": v(15, -140) * mm});
            skPoint(sketch, "E26.9.0.2", {"position": v(30, -140) * mm});
            skPoint(sketch, "E26.9.0.3", {"position": v(45, -140) * mm});
            skPoint(sketch, "E26.9.0.4", {"position": v(60, -140) * mm});
            skPoint(sketch, "E26.9.0.5", {"position": v(75, -140) * mm});
            skPoint(sketch, "E26.9.0.6", {"position": v(90, -140) * mm});
            skPoint(sketch, "E26.10.0.0", {"position": v(0, -155) * mm});
            skPoint(sketch, "E26.10.0.1", {"position": v(15, -155) * mm});
            skPoint(sketch, "E26.10.0.2", {"position": v(30, -155) * mm});
            skPoint(sketch, "E26.10.0.3", {"position": v(45, -155) * mm});
            skPoint(sketch, "E26.10.0.4", {"position": v(60, -155) * mm});
            skPoint(sketch, "E26.10.0.5", {"position": v(75, -155) * mm});
            skPoint(sketch, "E26.10.0.6", {"position": v(90, -155) * mm});
            skPoint(sketch, "E26.11.0.0", {"position": v(0, -170) * mm});
            skPoint(sketch, "E26.11.0.1", {"position": v(15, -170) * mm});
            skPoint(sketch, "E26.11.0.2", {"position": v(30, -170) * mm});
            skPoint(sketch, "E26.11.0.3", {"position": v(45, -170) * mm});
            skPoint(sketch, "E26.11.0.4", {"position": v(60, -170) * mm});
            skPoint(sketch, "E26.11.0.5", {"position": v(75, -170) * mm});
            skPoint(sketch, "E26.11.0.6", {"position": v(90, -170) * mm});
            skPoint(sketch, "E26.12.0.0", {"position": v(0, -185) * mm});
            skPoint(sketch, "E26.12.0.1", {"position": v(15, -185) * mm});
            skPoint(sketch, "E26.12.0.2", {"position": v(30, -185) * mm});
            skPoint(sketch, "E26.12.0.3", {"position": v(45, -185) * mm});
            skPoint(sketch, "E26.12.0.4", {"position": v(60, -185) * mm});
            skPoint(sketch, "E26.12.0.5", {"position": v(75, -185) * mm});
            skPoint(sketch, "E26.12.0.6", {"position": v(90, -185) * mm});
            skPoint(sketch, "E26.13.0.0", {"position": v(0, -200) * mm});
            skPoint(sketch, "E26.13.0.1", {"position": v(15, -200) * mm});
            skPoint(sketch, "E26.13.0.2", {"position": v(30, -200) * mm});
            skPoint(sketch, "E26.13.0.3", {"position": v(45, -200) * mm});
            skPoint(sketch, "E26.13.0.4", {"position": v(60, -200) * mm});
            skPoint(sketch, "E26.13.0.5", {"position": v(75, -200) * mm});
            skPoint(sketch, "E26.13.0.6", {"position": v(90, -200) * mm});
            skPoint(sketch, "E26.14.0.0", {"position": v(0, -215) * mm});
            skPoint(sketch, "E26.14.0.1", {"position": v(15, -215) * mm});
            skPoint(sketch, "E26.14.0.2", {"position": v(30, -215) * mm});
            skPoint(sketch, "E26.14.0.3", {"position": v(45, -215) * mm});
            skPoint(sketch, "E26.14.0.4", {"position": v(60, -215) * mm});
            skPoint(sketch, "E26.14.0.5", {"position": v(75, -215) * mm});
            skPoint(sketch, "E26.14.0.6", {"position": v(90, -215) * mm});
            skPoint(sketch, "E26.15.0.0", {"position": v(0, -230) * mm});
            skPoint(sketch, "E26.15.0.1", {"position": v(15, -230) * mm});
            skPoint(sketch, "E26.15.0.2", {"position": v(30, -230) * mm});
            skPoint(sketch, "E26.15.0.3", {"position": v(45, -230) * mm});
            skPoint(sketch, "E26.15.0.4", {"position": v(60, -230) * mm});
            skPoint(sketch, "E26.15.0.5", {"position": v(75, -230) * mm});
            skPoint(sketch, "E26.15.0.6", {"position": v(90, -230) * mm});
            skPoint(sketch, "E26.16.0.0", {"position": v(0, -245) * mm});
            skPoint(sketch, "E26.16.0.1", {"position": v(15, -245) * mm});
            skPoint(sketch, "E26.16.0.2", {"position": v(30, -245) * mm});
            skPoint(sketch, "E26.16.0.3", {"position": v(45, -245) * mm});
            skPoint(sketch, "E26.16.0.4", {"position": v(60, -245) * mm});
            skPoint(sketch, "E26.16.0.5", {"position": v(75, -245) * mm});
            skPoint(sketch, "E26.16.0.6", {"position": v(90, -245) * mm});
            skPoint(sketch, "E26.17.0.0", {"position": v(0, -260) * mm});
            skPoint(sketch, "E26.17.0.1", {"position": v(15, -260) * mm});
            skPoint(sketch, "E26.17.0.2", {"position": v(30, -260) * mm});
            skPoint(sketch, "E26.17.0.3", {"position": v(45, -260) * mm});
            skPoint(sketch, "E26.17.0.4", {"position": v(60, -260) * mm});
            skPoint(sketch, "E26.17.0.5", {"position": v(75, -260) * mm});
            skPoint(sketch, "E26.17.0.6", {"position": v(90, -260) * mm});
            skPoint(sketch, "E26.18.0.0", {"position": v(0, -275) * mm});
            skPoint(sketch, "E26.18.0.1", {"position": v(15, -275) * mm});
            skPoint(sketch, "E26.18.0.2", {"position": v(30, -275) * mm});
            skPoint(sketch, "E26.18.0.3", {"position": v(45, -275) * mm});
            skPoint(sketch, "E26.18.0.4", {"position": v(60, -275) * mm});
            skPoint(sketch, "E26.18.0.5", {"position": v(75, -275) * mm});
            skPoint(sketch, "E26.18.0.6", {"position": v(90, -275) * mm});
            skPoint(sketch, "E26.19.0.0", {"position": v(0, -290) * mm});
            skPoint(sketch, "E26.19.0.1", {"position": v(15, -290) * mm});
            skPoint(sketch, "E26.19.0.2", {"position": v(30, -290) * mm});
            skPoint(sketch, "E26.19.0.3", {"position": v(45, -290) * mm});
            skPoint(sketch, "E26.19.0.4", {"position": v(60, -290) * mm});
            skPoint(sketch, "E26.19.0.5", {"position": v(75, -290) * mm});
            skPoint(sketch, "E26.19.0.6", {"position": v(90, -290) * mm});
            skPoint(sketch, "E26.20.0.0", {"position": v(0, -305) * mm});
            skPoint(sketch, "E26.20.0.1", {"position": v(15, -305) * mm});
            skPoint(sketch, "E26.20.0.2", {"position": v(30, -305) * mm});
            skPoint(sketch, "E26.20.0.3", {"position": v(45, -305) * mm});
            skPoint(sketch, "E26.20.0.4", {"position": v(60, -305) * mm});
            skPoint(sketch, "E26.20.0.5", {"position": v(75, -305) * mm});
            skPoint(sketch, "E26.20.0.6", {"position": v(90, -305) * mm});
            skPoint(sketch, "E26.21.0.0", {"position": v(0, -320) * mm});
            skPoint(sketch, "E26.21.0.1", {"position": v(15, -320) * mm});
            skPoint(sketch, "E26.21.0.2", {"position": v(30, -320) * mm});
            skPoint(sketch, "E26.21.0.3", {"position": v(45, -320) * mm});
            skPoint(sketch, "E26.21.0.4", {"position": v(60, -320) * mm});
            skPoint(sketch, "E26.21.0.5", {"position": v(75, -320) * mm});
            skPoint(sketch, "E26.21.0.6", {"position": v(90, -320) * mm});
            skPoint(sketch, "E26.22.0.0", {"position": v(0, -335) * mm});
            skPoint(sketch, "E26.22.0.1", {"position": v(15, -335) * mm});
            skPoint(sketch, "E26.22.0.2", {"position": v(30, -335) * mm});
            skPoint(sketch, "E26.22.0.3", {"position": v(45, -335) * mm});
            skPoint(sketch, "E26.22.0.4", {"position": v(60, -335) * mm});
            skPoint(sketch, "E26.22.0.5", {"position": v(75, -335) * mm});
            skPoint(sketch, "E26.22.0.6", {"position": v(90, -335) * mm});
            skPoint(sketch, "E26.23.0.0", {"position": v(0, -350) * mm});
            skPoint(sketch, "E26.23.0.1", {"position": v(15, -350) * mm});
            skPoint(sketch, "E26.23.0.2", {"position": v(30, -350) * mm});
            skPoint(sketch, "E26.23.0.3", {"position": v(45, -350) * mm});
            skPoint(sketch, "E26.23.0.4", {"position": v(60, -350) * mm});
            skPoint(sketch, "E26.23.0.5", {"position": v(75, -350) * mm});
            skPoint(sketch, "E26.23.0.6", {"position": v(90, -350) * mm});
            skPoint(sketch, "E26.24.0.0", {"position": v(0, -365) * mm});
            skPoint(sketch, "E26.24.0.1", {"position": v(15, -365) * mm});
            skPoint(sketch, "E26.24.0.2", {"position": v(30, -365) * mm});
            skPoint(sketch, "E26.24.0.3", {"position": v(45, -365) * mm});
            skPoint(sketch, "E26.24.0.4", {"position": v(60, -365) * mm});
            skPoint(sketch, "E26.24.0.5", {"position": v(75, -365) * mm});
            skPoint(sketch, "E26.24.0.6", {"position": v(90, -365) * mm});
            skPoint(sketch, "E26.25.0.0", {"position": v(0, -380) * mm});
            skPoint(sketch, "E26.25.0.1", {"position": v(15, -380) * mm});
            skPoint(sketch, "E26.25.0.2", {"position": v(30, -380) * mm});
            skPoint(sketch, "E26.25.0.3", {"position": v(45, -380) * mm});
            skPoint(sketch, "E26.25.0.4", {"position": v(60, -380) * mm});
            skPoint(sketch, "E26.25.0.5", {"position": v(75, -380) * mm});
            skPoint(sketch, "E26.25.0.6", {"position": v(90, -380) * mm});
            skPoint(sketch, "E26.26.0.0", {"position": v(0, -395) * mm});
            skPoint(sketch, "E26.26.0.1", {"position": v(15, -395) * mm});
            skPoint(sketch, "E26.26.0.2", {"position": v(30, -395) * mm});
            skPoint(sketch, "E26.26.0.3", {"position": v(45, -395) * mm});
            skPoint(sketch, "E26.26.0.4", {"position": v(60, -395) * mm});
            skPoint(sketch, "E26.26.0.5", {"position": v(75, -395) * mm});
            skPoint(sketch, "E26.26.0.6", {"position": v(90, -395) * mm});
            skPoint(sketch, "E26.27.0.0", {"position": v(0, -410) * mm});
            skPoint(sketch, "E26.27.0.1", {"position": v(15, -410) * mm});
            skPoint(sketch, "E26.27.0.2", {"position": v(30, -410) * mm});
            skPoint(sketch, "E26.27.0.3", {"position": v(45, -410) * mm});
            skPoint(sketch, "E26.27.0.4", {"position": v(60, -410) * mm});
            skPoint(sketch, "E26.27.0.5", {"position": v(75, -410) * mm});
            skPoint(sketch, "E26.27.0.6", {"position": v(90, -410) * mm});
            skPoint(sketch, "E26.28.0.0", {"position": v(0, -425) * mm});
            skPoint(sketch, "E26.28.0.1", {"position": v(15, -425) * mm});
            skPoint(sketch, "E26.28.0.2", {"position": v(30, -425) * mm});
            skPoint(sketch, "E26.28.0.3", {"position": v(45, -425) * mm});
            skPoint(sketch, "E26.28.0.4", {"position": v(60, -425) * mm});
            skPoint(sketch, "E26.28.0.5", {"position": v(75, -425) * mm});
            skPoint(sketch, "E26.28.0.6", {"position": v(90, -425) * mm});
            skPoint(sketch, "E26.29.0.0", {"position": v(0, -440) * mm});
            skPoint(sketch, "E26.29.0.1", {"position": v(15, -440) * mm});
            skPoint(sketch, "E26.29.0.2", {"position": v(30, -440) * mm});
            skPoint(sketch, "E26.29.0.3", {"position": v(45, -440) * mm});
            skPoint(sketch, "E26.29.0.4", {"position": v(60, -440) * mm});
            skPoint(sketch, "E26.29.0.5", {"position": v(75, -440) * mm});
            skPoint(sketch, "E26.29.0.6", {"position": v(90, -440) * mm});
            skPoint(sketch, "E26.30.0.0", {"position": v(0, -455) * mm});
            skPoint(sketch, "E26.30.0.1", {"position": v(15, -455) * mm});
            skPoint(sketch, "E26.30.0.2", {"position": v(30, -455) * mm});
            skPoint(sketch, "E26.30.0.3", {"position": v(45, -455) * mm});
            skPoint(sketch, "E26.30.0.4", {"position": v(60, -455) * mm});
            skPoint(sketch, "E26.30.0.5", {"position": v(75, -455) * mm});
            skPoint(sketch, "E26.30.0.6", {"position": v(90, -455) * mm});
            skPoint(sketch, "E26.31.0.0", {"position": v(0, -470) * mm});
            skPoint(sketch, "E26.31.0.1", {"position": v(15, -470) * mm});
            skPoint(sketch, "E26.31.0.2", {"position": v(30, -470) * mm});
            skPoint(sketch, "E26.31.0.3", {"position": v(45, -470) * mm});
            skPoint(sketch, "E26.31.0.4", {"position": v(60, -470) * mm});
            skPoint(sketch, "E26.31.0.5", {"position": v(75, -470) * mm});
            skPoint(sketch, "E26.31.0.6", {"position": v(90, -470) * mm});
            skPoint(sketch, "E26.32.0.0", {"position": v(0, -485) * mm});
            skPoint(sketch, "E26.32.0.1", {"position": v(15, -485) * mm});
            skPoint(sketch, "E26.32.0.2", {"position": v(30, -485) * mm});
            skPoint(sketch, "E26.32.0.3", {"position": v(45, -485) * mm});
            skPoint(sketch, "E26.32.0.4", {"position": v(60, -485) * mm});
            skPoint(sketch, "E26.32.0.5", {"position": v(75, -485) * mm});
            skPoint(sketch, "E26.32.0.6", {"position": v(90, -485) * mm});
            skPoint(sketch, "E26.33.0.0", {"position": v(0, -500) * mm});
            skPoint(sketch, "E26.33.0.1", {"position": v(15, -500) * mm});
            skPoint(sketch, "E26.33.0.2", {"position": v(30, -500) * mm});
            skPoint(sketch, "E26.33.0.3", {"position": v(45, -500) * mm});
            skPoint(sketch, "E26.33.0.4", {"position": v(60, -500) * mm});
            skPoint(sketch, "E26.33.0.5", {"position": v(75, -500) * mm});
            skPoint(sketch, "E26.33.0.6", {"position": v(90, -500) * mm});
            skPoint(sketch, "E26.34.0.0", {"position": v(0, -515) * mm});
            skPoint(sketch, "E26.34.0.1", {"position": v(15, -515) * mm});
            skPoint(sketch, "E26.34.0.2", {"position": v(30, -515) * mm});
            skPoint(sketch, "E26.34.0.3", {"position": v(45, -515) * mm});
            skPoint(sketch, "E26.34.0.4", {"position": v(60, -515) * mm});
            skPoint(sketch, "E26.34.0.5", {"position": v(75, -515) * mm});
            skPoint(sketch, "E26.34.0.6", {"position": v(90, -515) * mm});
            skPoint(sketch, "E26.35.0.0", {"position": v(0, -530) * mm});
            skPoint(sketch, "E26.35.0.1", {"position": v(15, -530) * mm});
            skPoint(sketch, "E26.35.0.2", {"position": v(30, -530) * mm});
            skPoint(sketch, "E26.35.0.3", {"position": v(45, -530) * mm});
            skPoint(sketch, "E26.35.0.4", {"position": v(60, -530) * mm});
            skPoint(sketch, "E26.35.0.5", {"position": v(75, -530) * mm});
            skPoint(sketch, "E26.35.0.6", {"position": v(90, -530) * mm});
            skPoint(sketch, "E26.36.0.0", {"position": v(0, -545) * mm});
            skPoint(sketch, "E26.36.0.1", {"position": v(15, -545) * mm});
            skPoint(sketch, "E26.36.0.2", {"position": v(30, -545) * mm});
            skPoint(sketch, "E26.36.0.3", {"position": v(45, -545) * mm});
            skPoint(sketch, "E26.36.0.4", {"position": v(60, -545) * mm});
            skPoint(sketch, "E26.36.0.5", {"position": v(75, -545) * mm});
            skPoint(sketch, "E26.36.0.6", {"position": v(90, -545) * mm});
            skPoint(sketch, "E26.37.0.0", {"position": v(0, -560) * mm});
            skPoint(sketch, "E26.37.0.1", {"position": v(15, -560) * mm});
            skPoint(sketch, "E26.37.0.2", {"position": v(30, -560) * mm});
            skPoint(sketch, "E26.37.0.3", {"position": v(45, -560) * mm});
            skPoint(sketch, "E26.37.0.4", {"position": v(60, -560) * mm});
            skPoint(sketch, "E26.37.0.5", {"position": v(75, -560) * mm});
            skPoint(sketch, "E26.37.0.6", {"position": v(90, -560) * mm});
            skPoint(sketch, "E26.38.0.0", {"position": v(0, -575) * mm});
            skPoint(sketch, "E26.38.0.1", {"position": v(15, -575) * mm});
            skPoint(sketch, "E26.38.0.2", {"position": v(30, -575) * mm});
            skPoint(sketch, "E26.38.0.3", {"position": v(45, -575) * mm});
            skPoint(sketch, "E26.38.0.4", {"position": v(60, -575) * mm});
            skPoint(sketch, "E26.38.0.5", {"position": v(75, -575) * mm});
            skPoint(sketch, "E26.38.0.6", {"position": v(90, -575) * mm});
            skPoint(sketch, "E26.39.0.0", {"position": v(0, -590) * mm});
            skPoint(sketch, "E26.39.0.1", {"position": v(15, -590) * mm});
            skPoint(sketch, "E26.39.0.2", {"position": v(30, -590) * mm});
            skPoint(sketch, "E26.39.0.3", {"position": v(45, -590) * mm});
            skPoint(sketch, "E26.39.0.4", {"position": v(60, -590) * mm});
            skPoint(sketch, "E26.39.0.5", {"position": v(75, -590) * mm});
            skPoint(sketch, "E26.39.0.6", {"position": v(90, -590) * mm});
            skLineSegment(sketch, "E26.direction1", {"start": v(0, -5) * mm, "end": v(0, -20) * mm, "construction": true});
            skSolve(sketch);
        }
        {
            var Q0;
            Q0=sQuery(id+"F8.wireOp",VERTEX,"E24");
            var Q1;
            Q1=sQuery(id+"F8.wireOp",VERTEX,"E26.1.0.0");
            var Q2;
            Q2=sQuery(id+"F8.wireOp",VERTEX,"E26.2.0.0");
            var Q3;
            Q3=sQuery(id+"F8.wireOp",VERTEX,"E25.1.0.0");
            var Q4;
            Q4=sQuery(id+"F8.wireOp",VERTEX,"E26.1.0.1");
            var Q5;
            Q5=sQuery(id+"F8.wireOp",VERTEX,"E26.2.0.1");
            var Q6;
            Q6=sQuery(id+"F8.wireOp",VERTEX,"E26.3.0.1");
            var Q7;
            Q7=sQuery(id+"F8.wireOp",VERTEX,"E25.2.0.0");
            var Q8;
            Q8=sQuery(id+"F8.wireOp",VERTEX,"E25.3.0.0");
            var Q9;
            Q9=sQuery(id+"F8.wireOp",VERTEX,"E25.4.0.0");
            var Q10;
            Q10=sQuery(id+"F8.wireOp",VERTEX,"E25.5.0.0");
            var Q11;
            Q11=sQuery(id+"F8.wireOp",VERTEX,"E25.6.0.0");
            var Q12;
            Q12=sQuery(id+"F8.wireOp",VERTEX,"E26.1.0.4");
            var Q13;
            Q13=sQuery(id+"F8.wireOp",VERTEX,"E26.1.0.3");
            var Q14;
            Q14=sQuery(id+"F8.wireOp",VERTEX,"E26.1.0.2");
            var Q15;
            Q15=sQuery(id+"F8.wireOp",VERTEX,"E26.2.0.4");
            var Q16;
            Q16=sQuery(id+"F8.wireOp",VERTEX,"E26.4.0.6");
            var Q17;
            Q17=sQuery(id+"F8.wireOp",VERTEX,"E26.3.0.6");
            var Q18;
            Q18=sQuery(id+"F8.wireOp",VERTEX,"E26.3.0.3");
            var Q19;
            Q19=sQuery(id+"F8.wireOp",VERTEX,"E26.2.0.3");
            var Q20;
            Q20=sQuery(id+"F8.wireOp",VERTEX,"E26.3.0.5");
            var Q21;
            Q21=sQuery(id+"F8.wireOp",VERTEX,"E26.4.0.5");
            var Q22;
            Q22=sQuery(id+"F8.wireOp",VERTEX,"E26.3.0.2");
            var Q23;
            Q23=sQuery(id+"F8.wireOp",VERTEX,"E26.2.0.2");
            var Q24;
            Q24=sQuery(id+"F8.wireOp",VERTEX,"E26.4.0.4");
            var Q25;
            Q25=sQuery(id+"F8.wireOp",VERTEX,"E26.3.0.4");
            var Q26;
            Q26=sQuery(id+"F8.wireOp",VERTEX,"E26.4.0.3");
            var Q27;
            Q27=sQuery(id+"F8.wireOp",VERTEX,"E26.4.0.2");
            var Q28;
            Q28=sQuery(id+"F8.wireOp",VERTEX,"E26.2.0.6");
            var Q29;
            Q29=sQuery(id+"F8.wireOp",VERTEX,"E26.1.0.6");
            var Q30;
            Q30=sQuery(id+"F8.wireOp",VERTEX,"E26.1.0.5");
            var Q31;
            Q31=sQuery(id+"F8.wireOp",VERTEX,"E26.2.0.5");
            var Q32;
            Q32=sQuery(id+"F8.wireOp",VERTEX,"E26.6.0.6");
            var Q33;
            Q33=sQuery(id+"F8.wireOp",VERTEX,"E26.6.0.5");
            var Q34;
            Q34=sQuery(id+"F8.wireOp",VERTEX,"E26.6.0.4");
            var Q35;
            Q35=sQuery(id+"F8.wireOp",VERTEX,"E26.7.0.6");
            var Q36;
            Q36=sQuery(id+"F8.wireOp",VERTEX,"E26.7.0.5");
            var Q37;
            Q37=sQuery(id+"F8.wireOp",VERTEX,"E26.8.0.6");
            var Q38;
            Q38=sQuery(id+"F8.wireOp",VERTEX,"E26.8.0.5");
            var Q39;
            Q39=sQuery(id+"F8.wireOp",VERTEX,"E26.5.0.6");
            var Q40;
            Q40=sQuery(id+"F8.wireOp",VERTEX,"E26.5.0.5");
            var Q41;
            Q41=sQuery(id+"F8.wireOp",VERTEX,"E26.5.0.4");
            var Q42;
            Q42=sQuery(id+"F8.wireOp",VERTEX,"E26.5.0.3");
            var Q43;
            Q43=sQuery(id+"F8.wireOp",VERTEX,"E26.20.0.6");
            var Q44;
            Q44=sQuery(id+"F8.wireOp",VERTEX,"E26.19.0.6");
            var Q45;
            Q45=sQuery(id+"F8.wireOp",VERTEX,"E26.14.0.6");
            var Q46;
            Q46=sQuery(id+"F8.wireOp",VERTEX,"E26.13.0.6");
            var Q47;
            Q47=sQuery(id+"F8.wireOp",VERTEX,"E26.12.0.6");
            var Q48;
            Q48=sQuery(id+"F8.wireOp",VERTEX,"E26.23.0.6");
            var Q49;
            Q49=sQuery(id+"F8.wireOp",VERTEX,"E26.21.0.6");
            var Q50;
            Q50=sQuery(id+"F8.wireOp",VERTEX,"E26.22.0.6");
            var Q51;
            Q51=sQuery(id+"F8.wireOp",VERTEX,"E26.16.0.6");
            var Q52;
            Q52=sQuery(id+"F8.wireOp",VERTEX,"E26.15.0.6");
            var Q53;
            Q53=sQuery(id+"F8.wireOp",VERTEX,"E26.9.0.6");
            var Q54;
            Q54=sQuery(id+"F8.wireOp",VERTEX,"E26.24.0.6");
            var Q55;
            Q55=sQuery(id+"F8.wireOp",VERTEX,"E26.25.0.6");
            var Q56;
            Q56=sQuery(id+"F8.wireOp",VERTEX,"E26.17.0.6");
            var Q57;
            Q57=sQuery(id+"F8.wireOp",VERTEX,"E26.18.0.6");
            var Q58;
            Q58=sQuery(id+"F8.wireOp",VERTEX,"E26.26.0.6");
            var Q59;
            Q59=sQuery(id+"F8.wireOp",VERTEX,"E26.10.0.6");
            var Q60;
            Q60=sQuery(id+"F8.wireOp",VERTEX,"E26.11.0.6");
            var Q61;
            Q61=sQuery(id+"F8.wireOp",VERTEX,"E26.35.0.6");
            var Q62;
            Q62=sQuery(id+"F8.wireOp",VERTEX,"E26.36.0.6");
            var Q63;
            Q63=sQuery(id+"F8.wireOp",VERTEX,"E26.30.0.6");
            var Q64;
            Q64=sQuery(id+"F8.wireOp",VERTEX,"E26.29.0.6");
            var Q65;
            Q65=sQuery(id+"F8.wireOp",VERTEX,"E26.28.0.6");
            var Q66;
            Q66=sQuery(id+"F8.wireOp",VERTEX,"E26.37.0.6");
            var Q67;
            Q67=sQuery(id+"F8.wireOp",VERTEX,"E26.38.0.6");
            var Q68;
            Q68=sQuery(id+"F8.wireOp",VERTEX,"E26.39.0.6");
            var Q69;
            Q69=sQuery(id+"F8.wireOp",VERTEX,"E26.31.0.6");
            var Q70;
            Q70=sQuery(id+"F8.wireOp",VERTEX,"E26.32.0.6");
            var Q71;
            Q71=sQuery(id+"F8.wireOp",VERTEX,"E26.33.0.6");
            var Q72;
            Q72=sQuery(id+"F8.wireOp",VERTEX,"E26.34.0.6");
            var Q73;
            Q73=sQuery(id+"F8.wireOp",VERTEX,"E26.27.0.6");
            var Q74;
            Q74=sQuery(id+"F8.wireOp",VERTEX,"E26.27.0.6");
            var Q75;
            Q75=sQuery(id+"F8.wireOp",VERTEX,"E26.28.0.6");
            var Q76;
            Q76=sQuery(id+"F8.wireOp",VERTEX,"E26.29.0.6");
            var Q77;
            Q77=sQuery(id+"F8.wireOp",VERTEX,"E26.30.0.6");
            var Q78;
            Q78=sQuery(id+"F8.wireOp",VERTEX,"E26.31.0.6");
            var Q79;
            Q79=sQuery(id+"F8.wireOp",VERTEX,"E26.32.0.6");
            var Q80;
            Q80=sQuery(id+"F8.wireOp",VERTEX,"E26.33.0.6");
            var Q81;
            Q81=sQuery(id+"F8.wireOp",VERTEX,"E26.34.0.6");
            var Q82;
            Q82=sQuery(id+"F8.wireOp",VERTEX,"E26.35.0.6");
            var Q83;
            Q83=sQuery(id+"F8.wireOp",VERTEX,"E26.36.0.6");
            var Q84;
            Q84=sQuery(id+"F8.wireOp",VERTEX,"E26.37.0.6");
            var Q85;
            Q85=sQuery(id+"F8.wireOp",VERTEX,"E26.38.0.6");
            var Q86;
            Q86=sQuery(id+"F8.wireOp",VERTEX,"E26.39.0.6");
            var Q87;
            Q87=makeQuery(id+"F1.opExtrude","SWEPT_BODY",BODY,{"disambiguationData":[OSD([sQuery(id+"F0.wireOp",EDGE,"E1.bottom"),sQuery(id+"F0.wireOp",EDGE,"E1.top"),sQuery(id+"F0.wireOp",EDGE,"E1.left"),sQuery(id+"F0.wireOp",EDGE,"E1.right"),sQuery(id+"F0.wireOp",EDGE,"E2"),sQuery(id+"F0.wireOp",EDGE,"E3"),sQuery(id+"F0.wireOp",EDGE,"E4"),sQuery(id+"F0.wireOp",EDGE,"E5"),sQuery(id+"F0.wireOp",EDGE,"E6"),sQuery(id+"F0.wireOp",EDGE,"E7"),sQuery(id+"F0.wireOp",EDGE,"E8"),sQuery(id+"F0.wireOp",EDGE,"E9.MirrorCS"),sQuery(id+"F0.wireOp",EDGE,"E10.MirrorCS"),sQuery(id+"F0.wireOp",EDGE,"E11.MirrorCS"),sQuery(id+"F0.wireOp",EDGE,"E13.trimOffspring"),sQuery(id+"F0.wireOp",EDGE,"E14.trimOffspring"),sQuery(id+"F0.wireOp",EDGE,"E16.trimOffspring"),sQuery(id+"F0.wireOp",EDGE,"E17.trimOffspring"),sQuery(id+"F0.wireOp",EDGE,"E20"),sQuery(id+"F0.wireOp",EDGE,"E21")])]});
            var Q88;
            Q88=makeQuery(id+"F2.opExtrude","SWEPT_BODY",BODY,{"disambiguationData":[OSD([sQuery(id+"F0.wireOp",EDGE,"E23.1.0.1"),sQuery(id+"F0.wireOp",EDGE,"E23.1.0.2"),sQuery(id+"F0.wireOp",EDGE,"E23.1.0.3"),sQuery(id+"F0.wireOp",EDGE,"E23.1.0.4"),sQuery(id+"F0.wireOp",EDGE,"E23.1.0.11"),sQuery(id+"F0.wireOp",EDGE,"E23.1.0.12"),sQuery(id+"F0.wireOp",EDGE,"E23.1.0.13"),sQuery(id+"F0.wireOp",EDGE,"E23.1.0.14"),sQuery(id+"F0.wireOp",EDGE,"E23.1.0.15"),sQuery(id+"F0.wireOp",EDGE,"E23.1.0.16"),sQuery(id+"F0.wireOp",EDGE,"E23.1.0.18"),sQuery(id+"F0.wireOp",EDGE,"E23.1.0.19"),sQuery(id+"F0.wireOp",EDGE,"E23.1.0.20"),sQuery(id+"F0.wireOp",EDGE,"E23.1.0.21"),sQuery(id+"F0.wireOp",EDGE,"E23.1.0.22"),sQuery(id+"F0.wireOp",EDGE,"E23.1.0.23"),sQuery(id+"F0.wireOp",EDGE,"E23.1.0.24"),sQuery(id+"F0.wireOp",EDGE,"E23.1.0.25"),sQuery(id+"F0.wireOp",EDGE,"E23.1.0.26"),sQuery(id+"F0.wireOp",EDGE,"E23.1.0.27")])]});
            var Q89;
            Q89=makeQuery(id+"F3.opExtrude","SWEPT_BODY",BODY,{"disambiguationData":[OSD([sQuery(id+"F0.wireOp",EDGE,"E23.2.0.1"),sQuery(id+"F0.wireOp",EDGE,"E23.2.0.2"),sQuery(id+"F0.wireOp",EDGE,"E23.2.0.3"),sQuery(id+"F0.wireOp",EDGE,"E23.2.0.4"),sQuery(id+"F0.wireOp",EDGE,"E23.2.0.11"),sQuery(id+"F0.wireOp",EDGE,"E23.2.0.12"),sQuery(id+"F0.wireOp",EDGE,"E23.2.0.13"),sQuery(id+"F0.wireOp",EDGE,"E23.2.0.14"),sQuery(id+"F0.wireOp",EDGE,"E23.2.0.15"),sQuery(id+"F0.wireOp",EDGE,"E23.2.0.16"),sQuery(id+"F0.wireOp",EDGE,"E23.2.0.18"),sQuery(id+"F0.wireOp",EDGE,"E23.2.0.19"),sQuery(id+"F0.wireOp",EDGE,"E23.2.0.20"),sQuery(id+"F0.wireOp",EDGE,"E23.2.0.21"),sQuery(id+"F0.wireOp",EDGE,"E23.2.0.22"),sQuery(id+"F0.wireOp",EDGE,"E23.2.0.23"),sQuery(id+"F0.wireOp",EDGE,"E23.2.0.24"),sQuery(id+"F0.wireOp",EDGE,"E23.2.0.25"),sQuery(id+"F0.wireOp",EDGE,"E23.2.0.26"),sQuery(id+"F0.wireOp",EDGE,"E23.2.0.27")])]});
            var Q90;
            Q90=makeQuery(id+"F4.opExtrude","SWEPT_BODY",BODY,{"disambiguationData":[OSD([sQuery(id+"F0.wireOp",EDGE,"E23.3.0.1"),sQuery(id+"F0.wireOp",EDGE,"E23.3.0.2"),sQuery(id+"F0.wireOp",EDGE,"E23.3.0.3"),sQuery(id+"F0.wireOp",EDGE,"E23.3.0.4"),sQuery(id+"F0.wireOp",EDGE,"E23.3.0.11"),sQuery(id+"F0.wireOp",EDGE,"E23.3.0.12"),sQuery(id+"F0.wireOp",EDGE,"E23.3.0.13"),sQuery(id+"F0.wireOp",EDGE,"E23.3.0.14"),sQuery(id+"F0.wireOp",EDGE,"E23.3.0.15"),sQuery(id+"F0.wireOp",EDGE,"E23.3.0.16"),sQuery(id+"F0.wireOp",EDGE,"E23.3.0.18"),sQuery(id+"F0.wireOp",EDGE,"E23.3.0.19"),sQuery(id+"F0.wireOp",EDGE,"E23.3.0.20"),sQuery(id+"F0.wireOp",EDGE,"E23.3.0.21"),sQuery(id+"F0.wireOp",EDGE,"E23.3.0.22"),sQuery(id+"F0.wireOp",EDGE,"E23.3.0.23"),sQuery(id+"F0.wireOp",EDGE,"E23.3.0.24"),sQuery(id+"F0.wireOp",EDGE,"E23.3.0.25"),sQuery(id+"F0.wireOp",EDGE,"E23.3.0.26"),sQuery(id+"F0.wireOp",EDGE,"E23.3.0.27")])]});
            var Q91;
            Q91=makeQuery(id+"F5.opExtrude","SWEPT_BODY",BODY,{"disambiguationData":[OSD([sQuery(id+"F0.wireOp",EDGE,"E23.4.0.1"),sQuery(id+"F0.wireOp",EDGE,"E23.4.0.2"),sQuery(id+"F0.wireOp",EDGE,"E23.4.0.3"),sQuery(id+"F0.wireOp",EDGE,"E23.4.0.4"),sQuery(id+"F0.wireOp",EDGE,"E23.4.0.11"),sQuery(id+"F0.wireOp",EDGE,"E23.4.0.12"),sQuery(id+"F0.wireOp",EDGE,"E23.4.0.13"),sQuery(id+"F0.wireOp",EDGE,"E23.4.0.14"),sQuery(id+"F0.wireOp",EDGE,"E23.4.0.15"),sQuery(id+"F0.wireOp",EDGE,"E23.4.0.16"),sQuery(id+"F0.wireOp",EDGE,"E23.4.0.18"),sQuery(id+"F0.wireOp",EDGE,"E23.4.0.19"),sQuery(id+"F0.wireOp",EDGE,"E23.4.0.20"),sQuery(id+"F0.wireOp",EDGE,"E23.4.0.21"),sQuery(id+"F0.wireOp",EDGE,"E23.4.0.22"),sQuery(id+"F0.wireOp",EDGE,"E23.4.0.23"),sQuery(id+"F0.wireOp",EDGE,"E23.4.0.24"),sQuery(id+"F0.wireOp",EDGE,"E23.4.0.25"),sQuery(id+"F0.wireOp",EDGE,"E23.4.0.26"),sQuery(id+"F0.wireOp",EDGE,"E23.4.0.27")])]});
            var Q92;
            Q92=makeQuery(id+"F6.opExtrude","SWEPT_BODY",BODY,{"disambiguationData":[OSD([sQuery(id+"F0.wireOp",EDGE,"E23.5.0.1"),sQuery(id+"F0.wireOp",EDGE,"E23.5.0.2"),sQuery(id+"F0.wireOp",EDGE,"E23.5.0.3"),sQuery(id+"F0.wireOp",EDGE,"E23.5.0.4"),sQuery(id+"F0.wireOp",EDGE,"E23.5.0.11"),sQuery(id+"F0.wireOp",EDGE,"E23.5.0.12"),sQuery(id+"F0.wireOp",EDGE,"E23.5.0.13"),sQuery(id+"F0.wireOp",EDGE,"E23.5.0.14"),sQuery(id+"F0.wireOp",EDGE,"E23.5.0.15"),sQuery(id+"F0.wireOp",EDGE,"E23.5.0.16"),sQuery(id+"F0.wireOp",EDGE,"E23.5.0.18"),sQuery(id+"F0.wireOp",EDGE,"E23.5.0.19"),sQuery(id+"F0.wireOp",EDGE,"E23.5.0.20"),sQuery(id+"F0.wireOp",EDGE,"E23.5.0.21"),sQuery(id+"F0.wireOp",EDGE,"E23.5.0.22"),sQuery(id+"F0.wireOp",EDGE,"E23.5.0.23"),sQuery(id+"F0.wireOp",EDGE,"E23.5.0.24"),sQuery(id+"F0.wireOp",EDGE,"E23.5.0.25"),sQuery(id+"F0.wireOp",EDGE,"E23.5.0.26"),sQuery(id+"F0.wireOp",EDGE,"E23.5.0.27")])]});
            var Q93;
            Q93=makeQuery(id+"F7.opExtrude","SWEPT_BODY",BODY,{"disambiguationData":[OSD([sQuery(id+"F0.wireOp",EDGE,"E23.6.0.1"),sQuery(id+"F0.wireOp",EDGE,"E23.6.0.2"),sQuery(id+"F0.wireOp",EDGE,"E23.6.0.3"),sQuery(id+"F0.wireOp",EDGE,"E23.6.0.4"),sQuery(id+"F0.wireOp",EDGE,"E23.6.0.11"),sQuery(id+"F0.wireOp",EDGE,"E23.6.0.12"),sQuery(id+"F0.wireOp",EDGE,"E23.6.0.13"),sQuery(id+"F0.wireOp",EDGE,"E23.6.0.14"),sQuery(id+"F0.wireOp",EDGE,"E23.6.0.15"),sQuery(id+"F0.wireOp",EDGE,"E23.6.0.16"),sQuery(id+"F0.wireOp",EDGE,"E23.6.0.18"),sQuery(id+"F0.wireOp",EDGE,"E23.6.0.19"),sQuery(id+"F0.wireOp",EDGE,"E23.6.0.20"),sQuery(id+"F0.wireOp",EDGE,"E23.6.0.21"),sQuery(id+"F0.wireOp",EDGE,"E23.6.0.22"),sQuery(id+"F0.wireOp",EDGE,"E23.6.0.23"),sQuery(id+"F0.wireOp",EDGE,"E23.6.0.24"),sQuery(id+"F0.wireOp",EDGE,"E23.6.0.25"),sQuery(id+"F0.wireOp",EDGE,"E23.6.0.26"),sQuery(id+"F0.wireOp",EDGE,"E23.6.0.27")])]});
            hole(context, id + "F9", {"style" : HoleStyle.C_BORE, "endStyle" : HoleEndStyle.THROUGH, "holeDiameter" : 2.4 * mm, "cBoreDiameter" : 4.2 * mm, "cBoreDepth" : 2.3 * mm, "majorDiameter" : 5 * mm, "isTappedThrough" : true, "tappedDepth" : 12 * mm, "tapClearance" : 3, "locations" : qUnion([Q0, Q1, Q2, Q3, Q4, Q5, Q6, Q7, Q8, Q9, Q10, Q11, Q12, Q13, Q14, Q15, Q16, Q17, Q18, Q19, Q20, Q21, Q22, Q23, Q24, Q25, Q26, Q27, Q28, Q29, Q30, Q31, Q32, Q33, Q34, Q35, Q36, Q37, Q38, Q39, Q40, Q41, Q42, Q43, Q44, Q45, Q46, Q47, Q48, Q49, Q50, Q51, Q52, Q53, Q54, Q55, Q56, Q57, Q58, Q59, Q60, Q61, Q62, Q63, Q64, Q65, Q66, Q67, Q68, Q69, Q70, Q71, Q72, Q73, Q74, Q75, Q76, Q77, Q78, Q79, Q80, Q81, Q82, Q83, Q84, Q85, Q86]), "scope" : qUnion([Q87, Q88, Q89, Q90, Q91, Q92, Q93])});
        }
        {
            var Q0;
            Q0=qCreatedBy(makeId("Front.planeOp"),FACE);
            var sketch = newSketch(context, id + "F10", { "sketchPlane" : qUnion([Q0])});
            skLineSegment(sketch, "E27", {"start": v(-25, -2.4) * mm, "end": v(-25, 5.6) * mm, "construction": true});
            skLineSegment(sketch, "E28", {"start": v(-25, 5.6) * mm, "end": v(-33.5, 5.6) * mm});
            skLineSegment(sketch, "E29", {"start": v(-33.5, 5.6) * mm, "end": v(-33.5, -0.9) * mm});
            skLineSegment(sketch, "E30", {"start": v(-33.5, -0.9) * mm, "end": v(-28, -0.9) * mm});
            skLineSegment(sketch, "E31", {"start": v(-28, -0.9) * mm, "end": v(-28, 0.06) * mm});
            skLineSegment(sketch, "E32", {"start": v(-28, 2.4) * mm, "end": v(-25, 2.4) * mm});
            skPoint(sketch, "E33", {"position": v(-31, 5.6) * mm});
            skArc(sketch, "E34", {"start": v(-28, 1.61) * mm, "mid": v(-28.78, 0.84) * mm, "end": v(-28, 0.06) * mm});
            skLineSegment(sketch, "E35.MirrorCS", {"start": v(-25, 5.6) * mm, "end": v(-16.5, 5.6) * mm});
            skPoint(sketch, "E36.MirrorP", {"position": v(-19, 5.6) * mm});
            skLineSegment(sketch, "E37.MirrorCS", {"start": v(-16.5, 5.6) * mm, "end": v(-16.5, -0.9) * mm});
            skLineSegment(sketch, "E38.MirrorCS", {"start": v(-16.5, -0.9) * mm, "end": v(-22, -0.9) * mm});
            skArc(sketch, "E39.MirrorCS", {"start": v(-22, 1.61) * mm, "mid": v(-21.22, 0.84) * mm, "end": v(-22, 0.06) * mm});
            skLineSegment(sketch, "E40", {"start": v(-28, 0.06) * mm, "end": v(-28, 1.61) * mm});
            skLineSegment(sketch, "E41", {"start": v(-28, 1.61) * mm, "end": v(-28, 2.4) * mm});
            skLineSegment(sketch, "E42.MirrorCS", {"start": v(-22, 2.4) * mm, "end": v(-25, 2.4) * mm});
            skLineSegment(sketch, "E43.MirrorCS", {"start": v(-22, 1.61) * mm, "end": v(-22, 2.4) * mm});
            skLineSegment(sketch, "E44.MirrorCS", {"start": v(-22, -0.9) * mm, "end": v(-22, 0.06) * mm});
            skPoint(sketch, "E45", {"position": v(-25, 4.1) * mm});
            skLineSegment(sketch, "E46", {"start": v(-33.5, 5.1) * mm, "end": v(-16.5, 5.1) * mm});
            skLineSegment(sketch, "E47.MirrorCS", {"start": v(-22, 0.06) * mm, "end": v(-22, 1.61) * mm});
            skLineSegment(sketch, "E48", {"start": v(-3.22, 2.4) * mm, "end": v(-22, 2.4) * mm, "construction": true});
            skLineSegment(sketch, "E49", {"start": v(-2.6, 0.84) * mm, "end": v(-22, 0.84) * mm, "construction": true});
            skLineSegment(sketch, "E50", {"start": v(-3.22, -2.4) * mm, "end": v(-25, -2.4) * mm, "construction": true});
            skLineSegment(sketch, "E51.1.0.0", {"start": v(-45, -2.4) * mm, "end": v(-45, 5.6) * mm, "construction": true});
            skLineSegment(sketch, "E51.1.0.1", {"start": v(-48, -0.9) * mm, "end": v(-48, 0.06) * mm});
            skLineSegment(sketch, "E51.1.0.2", {"start": v(-48, 0.06) * mm, "end": v(-48, 1.61) * mm});
            skLineSegment(sketch, "E51.1.0.3", {"start": v(-48, 1.61) * mm, "end": v(-48, 2.4) * mm});
            skLineSegment(sketch, "E51.1.0.4", {"start": v(-48, 2.4) * mm, "end": v(-45, 2.4) * mm});
            skLineSegment(sketch, "E51.1.0.5", {"start": v(-42, 2.4) * mm, "end": v(-45, 2.4) * mm});
            skLineSegment(sketch, "E51.1.0.6", {"start": v(-42, 1.61) * mm, "end": v(-42, 2.4) * mm});
            skArc(sketch, "E51.1.0.7", {"start": v(-42, 1.61) * mm, "mid": v(-41.22, 0.84) * mm, "end": v(-42, 0.06) * mm});
            skLineSegment(sketch, "E51.1.0.8", {"start": v(-42, 0.06) * mm, "end": v(-42, 1.61) * mm});
            skLineSegment(sketch, "E51.1.0.9", {"start": v(-42, -0.9) * mm, "end": v(-42, 0.06) * mm});
            skLineSegment(sketch, "E51.1.0.10", {"start": v(-36.5, -0.9) * mm, "end": v(-42, -0.9) * mm});
            skLineSegment(sketch, "E51.1.0.11", {"start": v(-36.5, 5.6) * mm, "end": v(-36.5, -0.9) * mm});
            skLineSegment(sketch, "E51.1.0.12", {"start": v(-45, 5.6) * mm, "end": v(-36.5, 5.6) * mm});
            skLineSegment(sketch, "E51.1.0.13", {"start": v(-53.5, 5.1) * mm, "end": v(-36.5, 5.1) * mm});
            skPoint(sketch, "E51.1.0.14", {"position": v(-39, 5.6) * mm});
            skLineSegment(sketch, "E51.1.0.15", {"start": v(-45, 5.6) * mm, "end": v(-53.5, 5.6) * mm});
            skPoint(sketch, "E51.1.0.16", {"position": v(-51, 5.6) * mm});
            skLineSegment(sketch, "E51.1.0.17", {"start": v(-53.5, 5.6) * mm, "end": v(-53.5, -0.9) * mm});
            skLineSegment(sketch, "E51.1.0.18", {"start": v(-53.5, -0.9) * mm, "end": v(-48, -0.9) * mm});
            skArc(sketch, "E51.1.0.19", {"start": v(-48, 1.61) * mm, "mid": v(-48.77, 0.84) * mm, "end": v(-48, 0.06) * mm});
            skLineSegment(sketch, "E51.direction1", {"start": v(-25, -2.4) * mm, "end": v(-45, -2.4) * mm, "construction": true});
            skSolve(sketch);
        }
        {
            var Q0;
            {var subQ3=sQuery(id+"F10.wireOp",EDGE,"E30");Q0=makeQuery(id+"F10.imprint","IMPRINT",FACE,{"disambiguationData":[TD([[makeQuery(id+"F10.imprint","IMPRINT",EDGE,{"derivedFrom":subQ3}),1.0]])]});}
            var Q1;
            {var subQ4=sQuery(id+"F10.wireOp",EDGE,"E28");Q1=makeQuery(id+"F10.imprint","IMPRINT",FACE,{"disambiguationData":[TD([[makeQuery(id+"F10.imprint","IMPRINT",EDGE,{"derivedFrom":subQ4}),1.0]])]});}
            extrude(context, id + "F11", {"entities" : qUnion([Q0, Q1]), "depth" : (13.5 / 2) * mm, "offsetDistance" : 25 * mm});
        }
        {
            var Q0;
            Q0=makeQuery(id+"F11.opExtrude","CAP_FACE",FACE,{"disambiguationData":[OSD([sQuery(id+"F10.wireOp",EDGE,"E28"),sQuery(id+"F10.wireOp",EDGE,"E29"),sQuery(id+"F10.wireOp",EDGE,"E30"),sQuery(id+"F10.wireOp",EDGE,"E31"),sQuery(id+"F10.wireOp",EDGE,"E32"),sQuery(id+"F10.wireOp",EDGE,"E34"),sQuery(id+"F10.wireOp",EDGE,"E35.MirrorCS"),sQuery(id+"F10.wireOp",EDGE,"E37.MirrorCS"),sQuery(id+"F10.wireOp",EDGE,"E38.MirrorCS"),sQuery(id+"F10.wireOp",EDGE,"E39.MirrorCS"),sQuery(id+"F10.wireOp",EDGE,"E41"),sQuery(id+"F10.wireOp",EDGE,"E42.MirrorCS"),sQuery(id+"F10.wireOp",EDGE,"E43.MirrorCS"),sQuery(id+"F10.wireOp",EDGE,"E44.MirrorCS")])],"isStart":false});
            var sketch = newSketch(context, id + "F12", { "sketchPlane" : qUnion([Q0])});
            skLineSegment(sketch, "E52.0", {"start": v(-28, 0.06) * mm, "end": v(-28, 1.61) * mm});
            skLineSegment(sketch, "E52.1", {"start": v(-22, 0.06) * mm, "end": v(-22, 1.61) * mm});
            skLineSegment(sketch, "E52.2", {"start": v(-33.5, 5.1) * mm, "end": v(-16.5, 5.1) * mm});
            skSolve(sketch);
        }
        {
            var Q0;
            {var subQ1=sQuery(id+"F12.wireOp",EDGE,"E52.2");Q0=makeQuery(id+"F12.imprint","IMPRINT",FACE,{"disambiguationData":[TD([[makeQuery(id+"F12.imprint","IMPRINT",EDGE,{"derivedFrom":subQ1}),-1.0]])]});}
            var Q1;
            Q1=makeQuery(id+"F12.imprint","IMPRINT",FACE,{"disambiguationData":[TD([[makeQuery(id+"F12.imprint","IMPRINT",EDGE,{"derivedFrom":sQuery(id+"F12.wireOp",EDGE,"E52.0")}),1.0]])]});
            var Q2;
            Q2=makeQuery(id+"F12.imprint","IMPRINT",FACE,{"disambiguationData":[TD([[makeQuery(id+"F12.imprint","IMPRINT",EDGE,{"derivedFrom":sQuery(id+"F12.wireOp",EDGE,"E52.1")}),-1.0]])]});
            extrude(context, id + "F13", {"entities" : qUnion([Q0, Q1, Q2]), "operationType" : NewBodyOperationType.ADD, "depth" : ((22.5 - 12.5) / 2) * mm, "offsetDistance" : 25 * mm});
        }
        {
            var Q0;
            Q0=makeQuery(id+"F10.imprint","IMPRINT",FACE,{"disambiguationData":[TD([[makeQuery(id+"F10.imprint","IMPRINT",EDGE,{"derivedFrom":sQuery(id+"F10.wireOp",EDGE,"E51.1.0.1")}),1.0]])]});
            var Q1;
            {var subQ2=sQuery(id+"F10.wireOp",EDGE,"E51.1.0.12");Q1=makeQuery(id+"F10.imprint","IMPRINT",FACE,{"disambiguationData":[TD([[makeQuery(id+"F10.imprint","IMPRINT",EDGE,{"derivedFrom":subQ2}),-1.0]])]});}
            extrude(context, id + "F14", {"entities" : qUnion([Q0, Q1]), "depth" : (21.8 / 2) * mm, "offsetDistance" : 25 * mm});
        }
        {
            var Q0;
            Q0=makeQuery(id+"F14.opExtrude","CAP_FACE",FACE,{"disambiguationData":[OSD([sQuery(id+"F10.wireOp",EDGE,"E51.1.0.1"),sQuery(id+"F10.wireOp",EDGE,"E51.1.0.3"),sQuery(id+"F10.wireOp",EDGE,"E51.1.0.4"),sQuery(id+"F10.wireOp",EDGE,"E51.1.0.5"),sQuery(id+"F10.wireOp",EDGE,"E51.1.0.6"),sQuery(id+"F10.wireOp",EDGE,"E51.1.0.7"),sQuery(id+"F10.wireOp",EDGE,"E51.1.0.9"),sQuery(id+"F10.wireOp",EDGE,"E51.1.0.10"),sQuery(id+"F10.wireOp",EDGE,"E51.1.0.11"),sQuery(id+"F10.wireOp",EDGE,"E51.1.0.12"),sQuery(id+"F10.wireOp",EDGE,"E51.1.0.15"),sQuery(id+"F10.wireOp",EDGE,"E51.1.0.17"),sQuery(id+"F10.wireOp",EDGE,"E51.1.0.18"),sQuery(id+"F10.wireOp",EDGE,"E51.1.0.19")])],"isStart":false});
            var sketch = newSketch(context, id + "F15", { "sketchPlane" : qUnion([Q0])});
            skLineSegment(sketch, "E53.0", {"start": v(-48, 0.06) * mm, "end": v(-48, 1.61) * mm});
            skLineSegment(sketch, "E54.0", {"start": v(-53.5, 5.1) * mm, "end": v(-36.5, 5.1) * mm});
            skLineSegment(sketch, "E55.0", {"start": v(-42, 0.06) * mm, "end": v(-42, 1.61) * mm});
            skSolve(sketch);
        }
        {
            var Q0;
            {var subQ2=sQuery(id+"F15.wireOp",EDGE,"E54.0");Q0=makeQuery(id+"F15.imprint","IMPRINT",FACE,{"disambiguationData":[TD([[makeQuery(id+"F15.imprint","IMPRINT",EDGE,{"derivedFrom":subQ2}),-1.0]])]});}
            var Q1;
            Q1=makeQuery(id+"F15.imprint","IMPRINT",FACE,{"disambiguationData":[TD([[makeQuery(id+"F15.imprint","IMPRINT",EDGE,{"derivedFrom":sQuery(id+"F15.wireOp",EDGE,"E53.0")}),1.0]])]});
            var Q2;
            Q2=makeQuery(id+"F15.imprint","IMPRINT",FACE,{"disambiguationData":[TD([[makeQuery(id+"F15.imprint","IMPRINT",EDGE,{"derivedFrom":sQuery(id+"F15.wireOp",EDGE,"E55.0")}),-1.0]])]});
            extrude(context, id + "F16", {"entities" : qUnion([Q0, Q1, Q2]), "operationType" : NewBodyOperationType.ADD, "depth" : ((30.8 - 21.8) / 2) * mm, "offsetDistance" : 25 * mm});
        }
        {
            var Q0;
            Q0=makeQuery(id+"F11.opExtrude","SWEPT_FACE",FACE,{"disambiguationData":[OSD([sQuery(id+"F10.wireOp",EDGE,"E28"),sQuery(id+"F10.wireOp",EDGE,"E35.MirrorCS")])]});
            var sketch = newSketch(context, id + "F17", { "sketchPlane" : qUnion([Q0])});
            skPoint(sketch, "E56", {"position": v(-51, -6.5) * mm});
            skPoint(sketch, "E57", {"position": v(-39, -6.5) * mm});
            skPoint(sketch, "E58", {"position": v(-31, -4) * mm});
            skPoint(sketch, "E59", {"position": v(-19, -4) * mm});
            skSolve(sketch);
        }
        {
            var Q0;
            Q0=sQuery(id+"F17.wireOp",VERTEX,"E58");
            var Q1;
            Q1=sQuery(id+"F17.wireOp",VERTEX,"E59");
            var Q2;
            Q2=sQuery(id+"F17.wireOp",VERTEX,"E57");
            var Q3;
            Q3=sQuery(id+"F17.wireOp",VERTEX,"E56");
            var Q4;
            Q4=makeQuery(id+"F11.opExtrude","SWEPT_BODY",BODY,{"disambiguationData":[OSD([sQuery(id+"F10.wireOp",EDGE,"E28"),sQuery(id+"F10.wireOp",EDGE,"E29"),sQuery(id+"F10.wireOp",EDGE,"E30"),sQuery(id+"F10.wireOp",EDGE,"E31"),sQuery(id+"F10.wireOp",EDGE,"E32"),sQuery(id+"F10.wireOp",EDGE,"E34"),sQuery(id+"F10.wireOp",EDGE,"E35.MirrorCS"),sQuery(id+"F10.wireOp",EDGE,"E37.MirrorCS"),sQuery(id+"F10.wireOp",EDGE,"E38.MirrorCS"),sQuery(id+"F10.wireOp",EDGE,"E39.MirrorCS"),sQuery(id+"F10.wireOp",EDGE,"E41"),sQuery(id+"F10.wireOp",EDGE,"E42.MirrorCS"),sQuery(id+"F10.wireOp",EDGE,"E43.MirrorCS"),sQuery(id+"F10.wireOp",EDGE,"E44.MirrorCS")])]});
            var Q5;
            Q5=makeQuery(id+"F14.opExtrude","SWEPT_BODY",BODY,{"disambiguationData":[OSD([sQuery(id+"F10.wireOp",EDGE,"E51.1.0.1"),sQuery(id+"F10.wireOp",EDGE,"E51.1.0.3"),sQuery(id+"F10.wireOp",EDGE,"E51.1.0.4"),sQuery(id+"F10.wireOp",EDGE,"E51.1.0.5"),sQuery(id+"F10.wireOp",EDGE,"E51.1.0.6"),sQuery(id+"F10.wireOp",EDGE,"E51.1.0.7"),sQuery(id+"F10.wireOp",EDGE,"E51.1.0.9"),sQuery(id+"F10.wireOp",EDGE,"E51.1.0.10"),sQuery(id+"F10.wireOp",EDGE,"E51.1.0.11"),sQuery(id+"F10.wireOp",EDGE,"E51.1.0.12"),sQuery(id+"F10.wireOp",EDGE,"E51.1.0.15"),sQuery(id+"F10.wireOp",EDGE,"E51.1.0.17"),sQuery(id+"F10.wireOp",EDGE,"E51.1.0.18"),sQuery(id+"F10.wireOp",EDGE,"E51.1.0.19")])]});
            hole(context, id + "F18", {"style" : HoleStyle.SIMPLE, "endStyle" : HoleEndStyle.BLIND, "holeDiameter" : 2 * mm, "majorDiameter" : 5 * mm, "holeDepth" : 2.5 * mm, "isTappedThrough" : true, "tappedDepth" : 2.6 * mm, "tapClearance" : 3, "locations" : qUnion([Q0, Q1, Q2, Q3]), "scope" : qUnion([Q4, Q5])});
        }
        {
            var Q0;
            Q0=makeQuery(id+"F11.opExtrude","CAP_EDGE",EDGE,{"disambiguationData":[OSD([sQuery(id+"F10.wireOp",EDGE,"E28"),sQuery(id+"F10.wireOp",EDGE,"E35.MirrorCS")])],"isStart":false});
            var Q1;
            Q1=makeQuery(id+"F11.opExtrude","SWEPT_EDGE",EDGE,{"disambiguationData":[OSD([sQuery(id+"F10.wireOp",EDGE,"E35.MirrorCS"),sQuery(id+"F10.wireOp",EDGE,"E37.MirrorCS")])]});
            var Q2;
            Q2=makeQuery(id+"F13.opExtrude","CAP_EDGE",EDGE,{"disambiguationData":[OSD([sQuery(id+"F12.wireOp",EDGE,"E52.2")])],"isStart":false});
            var Q3;
            Q3=makeQuery(id+"F16.opExtrude","CAP_EDGE",EDGE,{"disambiguationData":[OSD([sQuery(id+"F15.wireOp",EDGE,"E54.0")])],"isStart":false});
            var Q4;
            Q4=makeQuery(id+"F14.opExtrude","CAP_EDGE",EDGE,{"disambiguationData":[OSD([sQuery(id+"F10.wireOp",EDGE,"E51.1.0.12"),sQuery(id+"F10.wireOp",EDGE,"E51.1.0.15")])],"isStart":false});
            var Q5;
            Q5=makeQuery(id+"F14.opExtrude","SWEPT_EDGE",EDGE,{"disambiguationData":[OSD([sQuery(id+"F10.wireOp",EDGE,"E51.1.0.11"),sQuery(id+"F10.wireOp",EDGE,"E51.1.0.12")])]});
            var Q6;
            Q6=makeQuery(id+"F11.opExtrude","SWEPT_EDGE",EDGE,{"disambiguationData":[OSD([sQuery(id+"F10.wireOp",EDGE,"E28"),sQuery(id+"F10.wireOp",EDGE,"E29")])]});
            var Q7;
            Q7=makeQuery(id+"F14.opExtrude","SWEPT_EDGE",EDGE,{"disambiguationData":[OSD([sQuery(id+"F10.wireOp",EDGE,"E51.1.0.15"),sQuery(id+"F10.wireOp",EDGE,"E51.1.0.17")])]});
            chamfer(context, id + "F19", {"entities" : qUnion([Q0, Q1, Q2, Q3, Q4, Q5, Q6, Q7]), "width" : 0.5 * mm, "tangentPropagation" : true});
        }
        {
            var Q0;
            Q0=makeQuery(id+"F14.opExtrude","SWEPT_BODY",BODY,{"disambiguationData":[OSD([sQuery(id+"F10.wireOp",EDGE,"E51.1.0.1"),sQuery(id+"F10.wireOp",EDGE,"E51.1.0.3"),sQuery(id+"F10.wireOp",EDGE,"E51.1.0.4"),sQuery(id+"F10.wireOp",EDGE,"E51.1.0.5"),sQuery(id+"F10.wireOp",EDGE,"E51.1.0.6"),sQuery(id+"F10.wireOp",EDGE,"E51.1.0.7"),sQuery(id+"F10.wireOp",EDGE,"E51.1.0.9"),sQuery(id+"F10.wireOp",EDGE,"E51.1.0.10"),sQuery(id+"F10.wireOp",EDGE,"E51.1.0.11"),sQuery(id+"F10.wireOp",EDGE,"E51.1.0.12"),sQuery(id+"F10.wireOp",EDGE,"E51.1.0.15"),sQuery(id+"F10.wireOp",EDGE,"E51.1.0.17"),sQuery(id+"F10.wireOp",EDGE,"E51.1.0.18"),sQuery(id+"F10.wireOp",EDGE,"E51.1.0.19")])]});
            var Q1;
            Q1=makeQuery(id+"F11.opExtrude","SWEPT_BODY",BODY,{"disambiguationData":[OSD([sQuery(id+"F10.wireOp",EDGE,"E28"),sQuery(id+"F10.wireOp",EDGE,"E29"),sQuery(id+"F10.wireOp",EDGE,"E30"),sQuery(id+"F10.wireOp",EDGE,"E31"),sQuery(id+"F10.wireOp",EDGE,"E32"),sQuery(id+"F10.wireOp",EDGE,"E34"),sQuery(id+"F10.wireOp",EDGE,"E35.MirrorCS"),sQuery(id+"F10.wireOp",EDGE,"E37.MirrorCS"),sQuery(id+"F10.wireOp",EDGE,"E38.MirrorCS"),sQuery(id+"F10.wireOp",EDGE,"E39.MirrorCS"),sQuery(id+"F10.wireOp",EDGE,"E41"),sQuery(id+"F10.wireOp",EDGE,"E42.MirrorCS"),sQuery(id+"F10.wireOp",EDGE,"E43.MirrorCS"),sQuery(id+"F10.wireOp",EDGE,"E44.MirrorCS")])]});
            var Q2;
            Q2=makeQuery(id+"F11.opExtrude","CAP_FACE",FACE,{"disambiguationData":[OSD([sQuery(id+"F10.wireOp",EDGE,"E28"),sQuery(id+"F10.wireOp",EDGE,"E29"),sQuery(id+"F10.wireOp",EDGE,"E30"),sQuery(id+"F10.wireOp",EDGE,"E31"),sQuery(id+"F10.wireOp",EDGE,"E32"),sQuery(id+"F10.wireOp",EDGE,"E34"),sQuery(id+"F10.wireOp",EDGE,"E35.MirrorCS"),sQuery(id+"F10.wireOp",EDGE,"E37.MirrorCS"),sQuery(id+"F10.wireOp",EDGE,"E38.MirrorCS"),sQuery(id+"F10.wireOp",EDGE,"E39.MirrorCS"),sQuery(id+"F10.wireOp",EDGE,"E41"),sQuery(id+"F10.wireOp",EDGE,"E42.MirrorCS"),sQuery(id+"F10.wireOp",EDGE,"E43.MirrorCS"),sQuery(id+"F10.wireOp",EDGE,"E44.MirrorCS")])],"isStart":true});
            mirror(context, id + "F20", {"operationType" : NewBodyOperationType.ADD, "entities" : qUnion([Q0, Q1]), "mirrorPlane" : qUnion([Q2])});
        }
    });
